FCSTD DOCUMENT  (FreeCAD 0.21R33110 (Git))
Label: FH36W-11S-0.3SHW_1x11-FlatCable
License: All rights reserved
LicenseURL: http://en.wikipedia.org/wiki/All_rights_reserved
objects: Sketcher::SketchObject×17, App::Annotation×2, Part::Part2DObjectPython×2, Image::ImagePlane×1, App::DocumentObjectGroup×1
note: 19 computed .brp shape members not serialized (recipe doc carries the construction recipe); baked Part::Feature solids carry a one-line shape summary decoded from their .brp

FEATURE [Sketcher::SketchObject] Sketch  label="Edge_Cuts_0.05"
  FullyConstrained = true
  Placement = pos=(0,0,0.2) rot=(0,0,1;0rad)
  sketch-geometry (33):
    g0: LineSegment StartX=-2.1 StartY=-2 StartZ=0 EndX=-2.1 EndY=-1.5 EndZ=0
    g1: ArcOfCircle CenterX=-1.9 CenterY=-1.5 CenterZ=0 NormalX=0 NormalY=0 NormalZ=1 AngleXU=0 Radius=0.2 StartAngle=1.5708 EndAngle=3.14159
    g2: ArcOfCircle CenterX=-1.9 CenterY=-1.1 CenterZ=0 NormalX=0 NormalY=0 NormalZ=1 AngleXU=0 Radius=0.2 StartAngle=4.71239 EndAngle=6.28319
    g3: LineSegment StartX=-1.7 StartY=-1.1 StartZ=0 EndX=-1.7 EndY=-0.75 EndZ=0
    g4: ArcOfCircle CenterX=-1.9 CenterY=-0.75 CenterZ=0 NormalX=0 NormalY=0 NormalZ=1 AngleXU=0 Radius=0.2 StartAngle=3e-16 EndAngle=1.5708
    g5: LineSegment StartX=-1.9 StartY=-0.55 StartZ=0 EndX=-2.22 EndY=-0.55 EndZ=0
    g6: ArcOfCircle CenterX=-2.22 CenterY=-0.35 CenterZ=0 NormalX=0 NormalY=0 NormalZ=1 AngleXU=0 Radius=0.2 StartAngle=2.34728 EndAngle=4.71239
    g7: LineSegment StartX=-2.36015 StartY=-0.207323 StartZ=0 EndX=-2.25836 EndY=-0.107324 EndZ=0
    g8: ArcOfCircle CenterX=-2.1182 CenterY=-0.25 CenterZ=0 NormalX=0 NormalY=0 NormalZ=1 AngleXU=0 Radius=0.2 StartAngle=1.5708 EndAngle=2.34728
    g9: ArcOfCircle CenterX=-2 CenterY=0.15 CenterZ=0 NormalX=0 NormalY=0 NormalZ=1 AngleXU=0 Radius=0.2 StartAngle=4.71239 EndAngle=6.28319
    g10: LineSegment StartX=-1.8 StartY=0.15 StartZ=0 EndX=-1.8 EndY=0.9 EndZ=0
    g11: ArcOfCircle CenterX=-1.6 CenterY=0.9 CenterZ=0 NormalX=0 NormalY=0 NormalZ=1 AngleXU=0 Radius=0.2 StartAngle=1.5708 EndAngle=3.14159
    g12: LineSegment StartX=-1.6 StartY=1.1 StartZ=0 EndX=1.6 EndY=1.1 EndZ=0
    g13: ArcOfCircle CenterX=1.6 CenterY=0.9 CenterZ=0 NormalX=0 NormalY=0 NormalZ=1 AngleXU=0 Radius=0.2 StartAngle=1e-16 EndAngle=1.5708
    g14: LineSegment StartX=1.8 StartY=0.9 StartZ=0 EndX=1.8 EndY=0.15 EndZ=0
    g15: ArcOfCircle CenterX=2 CenterY=0.15 CenterZ=0 NormalX=0 NormalY=0 NormalZ=1 AngleXU=0 Radius=0.2 StartAngle=3.14159 EndAngle=4.71239
    g16: LineSegment StartX=2 StartY=-0.05 StartZ=0 EndX=2.1182 EndY=-0.05 EndZ=0
    g17: ArcOfCircle CenterX=2.1182 CenterY=-0.25 CenterZ=0 NormalX=0 NormalY=0 NormalZ=1 AngleXU=0 Radius=0.2 StartAngle=0.794309 EndAngle=1.5708
    g18: LineSegment StartX=2.25836 StartY=-0.107324 StartZ=0 EndX=2.36016 EndY=-0.207324 EndZ=0
    g19: ArcOfCircle CenterX=2.22 CenterY=-0.35 CenterZ=0 NormalX=0 NormalY=0 NormalZ=1 AngleXU=0 Radius=0.2 StartAngle=4.71239 EndAngle=7.07749
    g20: LineSegment StartX=2.22 StartY=-0.55 StartZ=0 EndX=1.9 EndY=-0.55 EndZ=0
    g21: ArcOfCircle CenterX=1.9 CenterY=-0.75 CenterZ=0 NormalX=0 NormalY=0 NormalZ=1 AngleXU=0 Radius=0.2 StartAngle=1.5708 EndAngle=3.14159
    g22: LineSegment StartX=1.7 StartY=-1.1 StartZ=0 EndX=1.7 EndY=-0.75 EndZ=0
    g23: ArcOfCircle CenterX=1.9 CenterY=-1.1 CenterZ=0 NormalX=0 NormalY=0 NormalZ=1 AngleXU=0 Radius=0.2 StartAngle=3.14159 EndAngle=4.71239
    g24: ArcOfCircle CenterX=1.9 CenterY=-1.5 CenterZ=0 NormalX=0 NormalY=0 NormalZ=1 AngleXU=0 Radius=0.2 StartAngle=5e-16 EndAngle=1.5708
    g25: LineSegment StartX=2.1 StartY=-1.5 StartZ=0 EndX=2.1 EndY=-2 EndZ=0
    g26: LineSegment StartX=-2.42 StartY=0.15 StartZ=0 EndX=-2.42 EndY=-0.85 EndZ=0
    g27: LineSegment StartX=2.42 StartY=0.15 StartZ=0 EndX=2.42 EndY=-0.85 EndZ=0
    g28: LineSegment StartX=-2.1182 StartY=-0.05 StartZ=0 EndX=-2 EndY=-0.05 EndZ=0
    g29: LineSegment StartX=2.25836 StartY=-0.107324 StartZ=0 EndX=2.2 EndY=-0.05 EndZ=0
    g30: LineSegment StartX=2.1182 StartY=-0.05 StartZ=0 EndX=2.2 EndY=-0.05 EndZ=0
    g31: LineSegment StartX=-2.25836 StartY=-0.107324 StartZ=0 EndX=-2.2 EndY=-0.05 EndZ=0
    g32: LineSegment StartX=-2.1182 StartY=-0.05 StartZ=0 EndX=-2.2 EndY=-0.05 EndZ=0
  constraints (86):
    c: Vertical(g0)
    c: Vertical(g3)
    c: Horizontal(g5)
    c: Coincident(g8,g7)
    c: Vertical(g10)
    c: Vertical(g14)
    c: Horizontal(g16)
    c: Vertical(g22)
    c: Vertical(g25)
    c: Equal(g25,g0)
    c: Equal(g1,g24)
    c: Equal(g3,g22)
    c: Equal(g5,g20)
    c: Horizontal(g20)
    c: Equal(g18,g7)
    c: Equal(g17,g8)
    c: Equal(g9,g15)
    c: Radius(g1) = 0.2
    c: Equal(g1,g2)
    c: Equal(g2,g4)
    c: Equal(g4,g6)
    c: Equal(g8,g9)
    c: Equal(g11,g24)
    c: Equal(g24,g23)
    c: Equal(g23,g21)
    c: Equal(g21,g19)
    c: Equal(g19,g17)
    c: Tangent(g11,g12) = 1.5708
    c: Tangent(g10,g11) = 1.5708
    c: Tangent(g12,g13) = 1.5708
    c: Tangent(g13,g14) = 1.5708
    c: DistanceX(g10,g13) = 3.6
    c: Tangent(g14,g15) = -1.5708
    c: Tangent(g9,g10) = -1.5708
    c: DistanceY(g15,g12) = 1.15
    c: Symmetric(g11,g12,g-2)
    c: Tangent(g16,g17) = 1.5708
    c: Tangent(g17,g18) = 1.5708
    c: Tangent(g4,g5) = -1.5708
    c: Tangent(g3,g4) = -1.5708
    c: Tangent(g21,g22) = 1.5708
    c: Tangent(g20,g21) = -1.5708
    c: Tangent(g15,g16) = -1.5708
    c: DistanceX(g0,g25) = 4.2
    c: Tangent(g18,g19) = 1.5708
    c: Tangent(g19,g20) = 1.5708
    c: Tangent(g6,g7) = 1.5708
    c: Tangent(g5,g6) = 1.5708
    c: DistanceX(g3,g21) = 3.4
    c: Tangent(g2,g3) = -1.5708
    c: Tangent(g22,g23) = 1.5708
    c: Tangent(g23,g24) = 1.5708
    c: Tangent(g24,g25) = 1.5708
    c: Angle(g2) = 1.5708
    c: Tangent(g1,g2) = 1.5708
    c: Symmetric(g2,g23,g-2)
    c: Tangent(g0,g1) = 1.5708
    c: DistanceY(g5,g11) = 1.65
    c: Angle(g9) = 1.5708
    c: Symmetric(g9,g15,g-2)
    c: Vertical(g26)
    c: Vertical(g27)
    c: Equal(g26,g27)
    c: DistanceX(g26,g27) = 4.84
    c: Symmetric(g26,g27,g-2)
    c: Tangent(g6,g26)
    c: DistanceY(g23,g12) = 2.4
    c: DistanceY(g6,g26) = 0.5
    c: DistanceY(g26,g26) = 1
    c: DistanceY(g0,g0) = 0.5
    c: Coincident(g28,g8)
    c: Coincident(g28,g9)
    c: Horizontal(g28)
    c: Coincident(g29,g17)
    c: Tangent(g29,g17)
    c: Coincident(g30,g16)
    c: Coincident(g30,g29)
    c: Parallel(g30,g16)
    c: Coincident(g31,g7)
    c: Coincident(g32,g8)
    c: Coincident(g32,g31)
    c: Parallel(g31,g7)
    c: DistanceX(g31,g29) = 4.4
    c: Symmetric(g31,g29,g-2)
    c: Equal(g28,g16)
    c: DistanceY(g-1,g11) = 1.1
FEATURE [Sketcher::SketchObject] Sketch003  label="Pads_Poly_F_Cu_padNum=1"
  ExternalGeometry = -> [Sketch]
  FullyConstrained = true
  sketch-geometry (38):
    g0: LineSegment StartX=-1.73 StartY=0.65 StartZ=0 EndX=-1.73 EndY=0.15 EndZ=0
    g1: LineSegment StartX=-1.73 StartY=0.15 StartZ=0 EndX=-1.65 EndY=0.15 EndZ=0
    g2: LineSegment StartX=-1.65 StartY=0.15 StartZ=0 EndX=-1.65 EndY=-0.45 EndZ=0
    g3: LineSegment StartX=-1.65 StartY=-0.45 StartZ=0 EndX=-1.6 EndY=-0.6 EndZ=0
    g4: LineSegment StartX=-1.6 StartY=-0.6 StartZ=0 EndX=-1.6 EndY=-2 EndZ=0
    g5: LineSegment StartX=-1.6 StartY=-2 StartZ=0 EndX=-1.4 EndY=-2 EndZ=0
    g6: LineSegment StartX=-1.4 StartY=-2 StartZ=0 EndX=-1.4 EndY=-0.6 EndZ=0
    g7: LineSegment StartX=-1.4 StartY=-0.6 StartZ=0 EndX=-1.45 EndY=-0.45 EndZ=0
    g8: LineSegment StartX=-1.45 StartY=-0.45 StartZ=0 EndX=-1.45 EndY=0.2 EndZ=0
    g9: LineSegment StartX=-1.45 StartY=0.2 StartZ=0 EndX=-1.35 EndY=0.3 EndZ=0
    g10: LineSegment StartX=-1.35 StartY=0.3 StartZ=0 EndX=-1.35 EndY=0.85 EndZ=0
    g11: LineSegment StartX=-1.4 StartY=0.9 StartZ=0 EndX=-1.6 EndY=0.9 EndZ=0
    g12: LineSegment StartX=-1.65 StartY=0.85 StartZ=0 EndX=-1.65 EndY=0.65 EndZ=0
    g13: ArcOfCircle CenterX=-1.4 CenterY=0.85 CenterZ=0 NormalX=0 NormalY=0 NormalZ=1 AngleXU=0 Radius=0.05 StartAngle=6e-16 EndAngle=1.5708
    g14: LineSegment StartX=-1.65 StartY=0.65 StartZ=0 EndX=-1.73 EndY=0.65 EndZ=0
    g15: ArcOfCircle CenterX=-1.6 CenterY=0.85 CenterZ=0 NormalX=0 NormalY=0 NormalZ=1 AngleXU=0 Radius=0.05 StartAngle=1.5708 EndAngle=3.14159
    g16: GeomPoint X=-1.5 Y=0.9 Z=0
    g17: GeomPoint X=-1.5 Y=-2 Z=0
    g18: LineSegment StartX=1.6 StartY=-2 StartZ=0 EndX=1.6 EndY=-0.6 EndZ=0
    g19: LineSegment StartX=1.6 StartY=-0.6 StartZ=0 EndX=1.65 EndY=-0.45 EndZ=0
    g20: LineSegment StartX=1.65 StartY=-0.45 StartZ=0 EndX=1.65 EndY=0.15 EndZ=0
    g21: LineSegment StartX=1.65 StartY=0.15 StartZ=0 EndX=1.73 EndY=0.15 EndZ=0
    g22: LineSegment StartX=1.73 StartY=0.15 StartZ=0 EndX=1.73 EndY=0.65 EndZ=0
    g23: LineSegment StartX=1.6 StartY=0.9 StartZ=0 EndX=1.4 EndY=0.9 EndZ=0
    g24: LineSegment StartX=1.73 StartY=0.65 StartZ=0 EndX=1.65 EndY=0.65 EndZ=0
    g25: LineSegment StartX=1.65 StartY=0.65 StartZ=0 EndX=1.65 EndY=0.85 EndZ=0
    g26: ArcOfCircle CenterX=1.6 CenterY=0.85 CenterZ=0 NormalX=0 NormalY=0 NormalZ=1 AngleXU=0 Radius=0.05 StartAngle=3e-16 EndAngle=1.5708
    g27: ArcOfCircle CenterX=1.4 CenterY=0.85 CenterZ=0 NormalX=0 NormalY=0 NormalZ=1 AngleXU=0 Radius=0.05 StartAngle=1.5708 EndAngle=3.14159
    g28: LineSegment StartX=1.35 StartY=0.85 StartZ=0 EndX=1.35 EndY=0.3 EndZ=0
    g29: LineSegment StartX=1.35 StartY=0.3 StartZ=0 EndX=1.45 EndY=0.2 EndZ=0
    g30: LineSegment StartX=1.45 StartY=0.2 StartZ=0 EndX=1.45 EndY=-0.45 EndZ=0
    g31: LineSegment StartX=1.45 StartY=-0.45 StartZ=0 EndX=1.4 EndY=-0.6 EndZ=0
    g32: LineSegment StartX=1.4 StartY=-0.6 StartZ=0 EndX=1.4 EndY=-2 EndZ=0
    g33: LineSegment StartX=1.4 StartY=-2 StartZ=0 EndX=1.6 EndY=-2 EndZ=0
    g34: LineSegment StartX=-1.5 StartY=-2 StartZ=0 EndX=0 EndY=-2 EndZ=0
    g35: GeomPoint X=1.5 Y=-2 Z=0
    g36: LineSegment StartX=0 StartY=-2 StartZ=0 EndX=1.5 EndY=-2 EndZ=0
    g37: Circle CenterX=-1.5 CenterY=-1.9 CenterZ=0 NormalX=0 NormalY=0 NormalZ=1 AngleXU=0 Radius=0.0625
  constraints (102):
    c: Vertical(g0)
    c: Coincident(g0,g1)
    c: Coincident(g1,g2)
    c: Vertical(g2)
    c: Coincident(g2,g3)
    c: Coincident(g3,g4)
    c: Vertical(g4)
    c: Coincident(g4,g5)
    c: Horizontal(g5)
    c: Coincident(g5,g6)
    c: Vertical(g6)
    c: Coincident(g6,g7)
    c: Coincident(g7,g8)
    c: Vertical(g8)
    c: Coincident(g8,g9)
    c: Coincident(g9,g10)
    c: Vertical(g10)
    c: Horizontal(g11)
    c: Tangent(g11,g13) = -1.5708
    c: Tangent(g10,g13) = -1.5708
    c: Vertical(g12)
    c: Coincident(g14,g12)
    c: Coincident(g14,g0)
    c: Horizontal(g14)
    c: Tangent(g11,g15) = -1.5708
    c: Tangent(g12,g15) = -1.5708
    c: Equal(g13,g15)
    c: Horizontal(g1)
    c: DistanceY(g0,g0) = 0.5
    c: Symmetric(g11,g11,g16)
    c: Radius(g15) = 0.05
    c: DistanceX(g5,g5) = 0.2
    c: DistanceX(g1,g8) = 0.2
    c: Parallel(g3,g7)
    c: DistanceX(g12,g10) = 0.3
    c: Vertical(g1,g12)
    c: Horizontal(g7,g2)
    c: DistanceY(g3,g2) = 0.15
    c: Symmetric(g4,g5,g17)
    c: DistanceX(g17,g-1) = 1.5
    c: Horizontal(g4,g-10)
    c: Horizontal(g0,g-6)
    c: DistanceX(g-5,g0) = 0.07
    c: DistanceY(g-9,g11) = 1.45
    c: DistanceY(g-9,g2) = 0.1
    c: DistanceX(g-5,g16) = 0.3
    c: DistanceY(g-9,g9) = 0.85
    c: DistanceY(g8,g9) = 0.1
    c: Vertical(g18)
    c: Coincident(g18,g19)
    c: Coincident(g19,g20)
    c: Vertical(g20)
    c: Coincident(g20,g21)
    c: Horizontal(g21)
    c: Coincident(g21,g22)
    c: Vertical(g22)
    c: Horizontal(g23)
    c: Coincident(g22,g24)
    c: Coincident(g24,g25)
    c: Vertical(g25)
    c: Tangent(g25,g26) = -1.5708
    c: Tangent(g23,g27) = -1.5708
    c: Vertical(g28)
    c: Coincident(g28,g29)
    c: Coincident(g29,g30)
    c: Vertical(g30)
    c: Coincident(g30,g31)
    c: Coincident(g31,g32)
    c: Vertical(g32)
    c: Coincident(g33,g32)
    c: Coincident(g33,g18)
    c: Horizontal(g33)
    c: Parallel(g19,g31)
    c: Tangent(g28,g27) = -1.5708
    c: Equal(g26,g27)
    c: Equal(g11,g23)
    c: Equal(g0,g22)
    c: Equal(g14,g24)
    c: Horizontal(g24)
    c: Vertical(g20,g24)
    c: Equal(g29,g9)
    c: Tangent(g23,g26) = -1.5708
    c: DistanceY(g29,g28) = 0.1
    c: Equal(g28,g10)
    c: Equal(g30,g8)
    c: Equal(g31,g7)
    c: Equal(g5,g33)
    c: Equal(g6,g32)
    c: Equal(g4,g18)
    c: Equal(g20,g2)
    c: Symmetric(g11,g23,g-2)
    c: Equal(g25,g12)
    c: Coincident(g34,g17)
    c: PointOnObject(g34,g-2)
    c: Horizontal(g34)
    c: Symmetric(g32,g18,g35)
    c: Coincident(g36,g34)
    c: Coincident(g36,g35)
    c: Horizontal(g36)
    c: Diameter(g37) = 0.125
    c: DistanceY(g17,g37) = 0.1
    c: DistanceX(g17,g37) = 0
FEATURE [Sketcher::SketchObject] Sketch005  label="Pads_Poly_F_Cu_padNum=11"
  FullyConstrained = false
  sketch-geometry (38):
    g0: LineSegment StartX=-1.73 StartY=0.65 StartZ=0 EndX=-1.73 EndY=0.15 EndZ=0
    g1: LineSegment StartX=-1.73 StartY=0.15 StartZ=0 EndX=-1.65 EndY=0.15 EndZ=0
    g2: LineSegment StartX=-1.65 StartY=0.15 StartZ=0 EndX=-1.65 EndY=-0.45 EndZ=0
    g3: LineSegment StartX=-1.65 StartY=-0.45 StartZ=0 EndX=-1.6 EndY=-0.6 EndZ=0
    g4: LineSegment StartX=-1.6 StartY=-0.6 StartZ=0 EndX=-1.6 EndY=-2 EndZ=0
    g5: LineSegment StartX=-1.6 StartY=-2 StartZ=0 EndX=-1.4 EndY=-2 EndZ=0
    g6: LineSegment StartX=-1.4 StartY=-2 StartZ=0 EndX=-1.4 EndY=-0.6 EndZ=0
    g7: LineSegment StartX=-1.4 StartY=-0.6 StartZ=0 EndX=-1.45 EndY=-0.45 EndZ=0
    g8: LineSegment StartX=-1.45 StartY=-0.45 StartZ=0 EndX=-1.45 EndY=0.2 EndZ=0
    g9: LineSegment StartX=-1.45 StartY=0.2 StartZ=0 EndX=-1.35 EndY=0.3 EndZ=0
    g10: LineSegment StartX=-1.35 StartY=0.3 StartZ=0 EndX=-1.35 EndY=0.85 EndZ=0
    g11: LineSegment StartX=-1.4 StartY=0.9 StartZ=0 EndX=-1.6 EndY=0.9 EndZ=0
    g12: LineSegment StartX=-1.65 StartY=0.85 StartZ=0 EndX=-1.65 EndY=0.65 EndZ=0
    g13: ArcOfCircle CenterX=-1.4 CenterY=0.85 CenterZ=0 NormalX=0 NormalY=0 NormalZ=1 AngleXU=0 Radius=0.05 StartAngle=6e-16 EndAngle=1.5708
    g14: LineSegment StartX=-1.65 StartY=0.65 StartZ=0 EndX=-1.73 EndY=0.65 EndZ=0
    g15: ArcOfCircle CenterX=-1.6 CenterY=0.85 CenterZ=0 NormalX=0 NormalY=0 NormalZ=1 AngleXU=0 Radius=0.05 StartAngle=1.5708 EndAngle=3.14159
    g16: GeomPoint X=-1.5 Y=0.9 Z=0
    g17: GeomPoint X=-1.5 Y=-2 Z=0
    g18: LineSegment StartX=1.6 StartY=-2 StartZ=0 EndX=1.6 EndY=-0.6 EndZ=0
    g19: LineSegment StartX=1.6 StartY=-0.6 StartZ=0 EndX=1.65 EndY=-0.45 EndZ=0
    g20: LineSegment StartX=1.65 StartY=-0.45 StartZ=0 EndX=1.65 EndY=0.15 EndZ=0
    g21: LineSegment StartX=1.65 StartY=0.15 StartZ=0 EndX=1.73 EndY=0.15 EndZ=0
    g22: LineSegment StartX=1.73 StartY=0.15 StartZ=0 EndX=1.73 EndY=0.65 EndZ=0
    g23: LineSegment StartX=1.6 StartY=0.9 StartZ=0 EndX=1.4 EndY=0.9 EndZ=0
    g24: LineSegment StartX=1.73 StartY=0.65 StartZ=0 EndX=1.65 EndY=0.65 EndZ=0
    g25: LineSegment StartX=1.65 StartY=0.65 StartZ=0 EndX=1.65 EndY=0.85 EndZ=0
    g26: ArcOfCircle CenterX=1.6 CenterY=0.85 CenterZ=0 NormalX=0 NormalY=0 NormalZ=1 AngleXU=0 Radius=0.05 StartAngle=3e-16 EndAngle=1.5708
    g27: ArcOfCircle CenterX=1.4 CenterY=0.85 CenterZ=0 NormalX=0 NormalY=0 NormalZ=1 AngleXU=0 Radius=0.05 StartAngle=1.5708 EndAngle=3.14159
    g28: LineSegment StartX=1.35 StartY=0.85 StartZ=0 EndX=1.35 EndY=0.3 EndZ=0
    g29: LineSegment StartX=1.35 StartY=0.3 StartZ=0 EndX=1.45 EndY=0.2 EndZ=0
    g30: LineSegment StartX=1.45 StartY=0.2 StartZ=0 EndX=1.45 EndY=-0.45 EndZ=0
    g31: LineSegment StartX=1.45 StartY=-0.45 StartZ=0 EndX=1.4 EndY=-0.6 EndZ=0
    g32: LineSegment StartX=1.4 StartY=-0.6 StartZ=0 EndX=1.4 EndY=-2 EndZ=0
    g33: LineSegment StartX=1.4 StartY=-2 StartZ=0 EndX=1.6 EndY=-2 EndZ=0
    g34: LineSegment StartX=-1.5 StartY=-2 StartZ=0 EndX=0 EndY=-2 EndZ=0
    g35: GeomPoint X=1.5 Y=-2 Z=0
    g36: LineSegment StartX=0 StartY=-2 StartZ=0 EndX=1.5 EndY=-2 EndZ=0
    g37: Circle CenterX=1.5 CenterY=-1.9 CenterZ=0 NormalX=0 NormalY=0 NormalZ=1 AngleXU=0 Radius=0.0625
  constraints (95):
    c: Vertical(g0)
    c: Coincident(g0,g1)
    c: Coincident(g1,g2)
    c: Vertical(g2)
    c: Coincident(g2,g3)
    c: Coincident(g3,g4)
    c: Vertical(g4)
    c: Coincident(g4,g5)
    c: Horizontal(g5)
    c: Coincident(g5,g6)
    c: Vertical(g6)
    c: Coincident(g6,g7)
    c: Coincident(g7,g8)
    c: Vertical(g8)
    c: Coincident(g8,g9)
    c: Coincident(g9,g10)
    c: Vertical(g10)
    c: Horizontal(g11)
    c: Tangent(g11,g13) = -1.5708
    c: Tangent(g10,g13) = -1.5708
    c: Vertical(g12)
    c: Coincident(g14,g12)
    c: Coincident(g14,g0)
    c: Horizontal(g14)
    c: Tangent(g11,g15) = -1.5708
    c: Tangent(g12,g15) = -1.5708
    c: Equal(g13,g15)
    c: Horizontal(g1)
    c: DistanceY(g0,g0) = 0.5
    c: Symmetric(g11,g11,g16)
    c: Radius(g15) = 0.05
    c: DistanceX(g5,g5) = 0.2
    c: DistanceX(g1,g8) = 0.2
    c: Parallel(g3,g7)
    c: DistanceX(g12,g10) = 0.3
    c: Vertical(g1,g12)
    c: Horizontal(g7,g2)
    c: DistanceY(g3,g2) = 0.15
    c: Symmetric(g4,g5,g17)
    c: DistanceX(g17,g-1) = 1.5
    c: DistanceY(g8,g9) = 0.1
    c: Vertical(g18)
    c: Coincident(g18,g19)
    c: Coincident(g19,g20)
    c: Vertical(g20)
    c: Coincident(g20,g21)
    c: Horizontal(g21)
    c: Coincident(g21,g22)
    c: Vertical(g22)
    c: Horizontal(g23)
    c: Coincident(g22,g24)
    c: Coincident(g24,g25)
    c: Vertical(g25)
    c: Tangent(g25,g26) = -1.5708
    c: Tangent(g23,g27) = -1.5708
    c: Vertical(g28)
    c: Coincident(g28,g29)
    c: Coincident(g29,g30)
    c: Vertical(g30)
    c: Coincident(g30,g31)
    c: Coincident(g31,g32)
    c: Vertical(g32)
    c: Coincident(g33,g32)
    c: Coincident(g33,g18)
    c: Horizontal(g33)
    c: Parallel(g19,g31)
    c: Tangent(g28,g27) = -1.5708
    c: Equal(g26,g27)
    c: Equal(g11,g23)
    c: Equal(g0,g22)
    c: Equal(g14,g24)
    c: Horizontal(g24)
    c: Vertical(g20,g24)
    c: Equal(g29,g9)
    c: Tangent(g23,g26) = -1.5708
    c: DistanceY(g29,g28) = 0.1
    c: Equal(g28,g10)
    c: Equal(g30,g8)
    c: Equal(g31,g7)
    c: Equal(g5,g33)
    c: Equal(g6,g32)
    c: Equal(g4,g18)
    c: Equal(g20,g2)
    c: Symmetric(g11,g23,g-2)
    c: Equal(g25,g12)
    c: Coincident(g34,g17)
    c: PointOnObject(g34,g-2)
    c: Horizontal(g34)
    c: Symmetric(g32,g18,g35)
    c: Coincident(g36,g34)
    c: Coincident(g36,g35)
    c: Horizontal(g36)
    c: Diameter(g37) = 0.125
    c: DistanceX(g37,g35) = 0
    c: DistanceY(g35,g37) = 0.1
FEATURE [App::Annotation] Text  label="Ref#_1.0mm"
  LabelText = REF**
  Position = (0,3,0)
FEATURE [App::Annotation] Text001  label="Value#_1.0mm"
  LabelText = Value 
  Position = (0,2,0)
FEATURE [Image::ImagePlane] pads_dimensions  label="pads-dimensions"
  Placement = pos=(-1.63,-0.68,-1) rot=(0,0,1;0rad)
  XSize = 6.21369
  YSize = 4.37753
FEATURE [Sketcher::SketchObject] Sketch006  label="Pads_Poly_F_Cu_padNum=2"
  ExternalGeometry = -> [Sketch003]
  FullyConstrained = false
  sketch-geometry (11):
    g0: LineSegment StartX=-1.29764 StartY=-2 StartZ=0 EndX=-1.29764 EndY=-0.593736 EndZ=0
    g1: LineSegment StartX=-1.29764 StartY=-0.593736 StartZ=0 EndX=-1.34764 EndY=-0.443736 EndZ=0
    g2: LineSegment StartX=-1.34764 StartY=-0.443736 StartZ=0 EndX=-1.34764 EndY=0.208373 EndZ=0
    g3: LineSegment StartX=-1.34764 StartY=0.208373 StartZ=0 EndX=-1.25602 EndY=0.3 EndZ=0
    g4: LineSegment StartX=-1.25602 StartY=0.3 StartZ=0 EndX=-1.13927 EndY=0.3 EndZ=0
    g5: LineSegment StartX=-1.13927 StartY=0.3 StartZ=0 EndX=-1.04764 EndY=0.208373 EndZ=0
    g6: LineSegment StartX=-1.04764 StartY=0.208373 StartZ=0 EndX=-1.04764 EndY=-0.443736 EndZ=0
    g7: LineSegment StartX=-1.04764 StartY=-0.443736 StartZ=0 EndX=-1.09764 EndY=-0.593736 EndZ=0
    g8: LineSegment StartX=-1.09764 StartY=-0.593736 StartZ=0 EndX=-1.09764 EndY=-2 EndZ=0
    g9: LineSegment StartX=-1.09764 StartY=-2 StartZ=0 EndX=-1.29764 EndY=-2 EndZ=0
    g10: Circle CenterX=-1.19764 CenterY=-1.9 CenterZ=0 NormalX=0 NormalY=0 NormalZ=1 AngleXU=0 Radius=0.0625
  constraints (29):
    c: Vertical(g0)
    c: Coincident(g0,g1)
    c: Coincident(g1,g2)
    c: Vertical(g2)
    c: Coincident(g2,g3)
    c: Coincident(g3,g4)
    c: Coincident(g4,g5)
    c: Coincident(g5,g6)
    c: Vertical(g6)
    c: Coincident(g6,g7)
    c: Coincident(g7,g8)
    c: Vertical(g8)
    c: Coincident(g8,g9)
    c: Coincident(g9,g0)
    c: Horizontal(g9)
    c: Horizontal(g4)
    c: Equal(g6,g2)
    c: Equal(g3,g5)
    c: Equal(g1,g7)
    c: Angle(g3) = 0.785398
    c: Angle(g5) = -0.785398
    c: DistanceY(g7,g6) = 0.15
    c: DistanceX(g9,g9) = 0.2
    c: DistanceX(g1,g6) = 0.3
    c: DistanceY(g-3,g0) = 0
    c: DistanceY(g0,g3) = 2.3
    c: Equal(g-4,g10)
    c: DistanceY(g0,g10) = 0.1
    c: DistanceX(g0,g10) = 0.1
FEATURE [Sketcher::SketchObject] Sketch007  label="Pads_Poly_F_Cu_padNum=3"
  FullyConstrained = false
  sketch-geometry (15):
    g0: ArcOfCircle CenterX=-1.00046 CenterY=0.85 CenterZ=0 NormalX=0 NormalY=0 NormalZ=1 AngleXU=0 Radius=0.05 StartAngle=1.57184 EndAngle=3.14159
    g1: LineSegment StartX=-1.05046 StartY=0.85 StartZ=0 EndX=-1.05046 EndY=0.3 EndZ=0
    g2: LineSegment StartX=-1.05046 StartY=0.3 StartZ=0 EndX=-0.961208 EndY=0.198248 EndZ=0
    g3: LineSegment StartX=-0.961208 StartY=0.198248 StartZ=0 EndX=-0.961208 EndY=-0.45 EndZ=0
    g4: LineSegment StartX=-0.961208 StartY=-0.45 StartZ=0 EndX=-1.00121 EndY=-0.601752 EndZ=0
    g5: LineSegment StartX=-1.00121 StartY=-0.601752 StartZ=0 EndX=-1.00121 EndY=-2 EndZ=0
    g6: LineSegment StartX=-1.00121 StartY=-2 StartZ=0 EndX=-0.801208 EndY=-2 EndZ=0
    g7: LineSegment StartX=-0.801208 StartY=-2 StartZ=0 EndX=-0.801208 EndY=-0.601752 EndZ=0
    g8: LineSegment StartX=-0.801208 StartY=-0.601752 StartZ=0 EndX=-0.841208 EndY=-0.45 EndZ=0
    g9: LineSegment StartX=-0.841208 StartY=-0.45 StartZ=0 EndX=-0.841208 EndY=0.2 EndZ=0
    g10: LineSegment StartX=-0.841208 StartY=0.2 StartZ=0 EndX=-0.75 EndY=0.3 EndZ=0
    g11: LineSegment StartX=-0.75 StartY=0.3 StartZ=0 EndX=-0.75 EndY=0.85 EndZ=0
    g12: ArcOfCircle CenterX=-0.8 CenterY=0.85 CenterZ=0 NormalX=0 NormalY=0 NormalZ=1 AngleXU=0 Radius=0.05 StartAngle=1e-15 EndAngle=1.5708
    g13: LineSegment StartX=-0.8 StartY=0.9 StartZ=0 EndX=-1.00051 EndY=0.9 EndZ=0
    g14: Circle CenterX=-0.9 CenterY=-1.9 CenterZ=0 NormalX=0 NormalY=0 NormalZ=1 AngleXU=0 Radius=0.0625
  constraints (29):
    c: Coincident(g0,g1)
    c: Vertical(g1)
    c: Coincident(g1,g2)
    c: Coincident(g2,g3)
    c: Vertical(g3)
    c: Coincident(g3,g4)
    c: Coincident(g4,g5)
    c: Vertical(g5)
    c: Horizontal(g6)
    c: Coincident(g6,g7)
    c: Vertical(g7)
    c: Coincident(g7,g8)
    c: Coincident(g8,g9)
    c: Vertical(g9)
    c: Coincident(g9,g10)
    c: Coincident(g10,g11)
    c: Coincident(g12,g13)
    c: Horizontal(g13)
    c: Coincident(g0,g13)
    c: Equal(g12,g0)
    c: Equal(g11,g1)
    c: DistanceY(g10,g1) = 0
    c: DistanceX(g2,g9) = 0.12
    c: Coincident(g6,g5)
    c: DistanceX(g6,g6) = 0.2
    c: DistanceY(g4,g7) = 0
    c: DistanceY(g3,g8) = 0
    c: Equal(g8,g4)
    c: Equal(g10,g2)
FEATURE [Sketcher::SketchObject] Sketch008  label="Pads_Poly_F_Cu_padNum=4"
  ExternalGeometry = -> [Sketch003]
  FullyConstrained = false
  sketch-geometry (11):
    g0: LineSegment StartX=-0.697644 StartY=-2 StartZ=0 EndX=-0.697644 EndY=-0.593736 EndZ=0
    g1: LineSegment StartX=-0.697644 StartY=-0.593736 StartZ=0 EndX=-0.747644 EndY=-0.443736 EndZ=0
    g2: LineSegment StartX=-0.747644 StartY=-0.443736 StartZ=0 EndX=-0.747644 EndY=0.208373 EndZ=0
    g3: LineSegment StartX=-0.747644 StartY=0.208373 StartZ=0 EndX=-0.656017 EndY=0.3 EndZ=0
    g4: LineSegment StartX=-0.656017 StartY=0.3 StartZ=0 EndX=-0.539272 EndY=0.3 EndZ=0
    g5: LineSegment StartX=-0.539272 StartY=0.3 StartZ=0 EndX=-0.447644 EndY=0.208373 EndZ=0
    g6: LineSegment StartX=-0.447644 StartY=0.208373 StartZ=0 EndX=-0.447644 EndY=-0.443736 EndZ=0
    g7: LineSegment StartX=-0.447644 StartY=-0.443736 StartZ=0 EndX=-0.497644 EndY=-0.593736 EndZ=0
    g8: LineSegment StartX=-0.497644 StartY=-0.593736 StartZ=0 EndX=-0.497644 EndY=-2 EndZ=0
    g9: LineSegment StartX=-0.497644 StartY=-2 StartZ=0 EndX=-0.697644 EndY=-2 EndZ=0
    g10: Circle CenterX=-0.597644 CenterY=-1.9 CenterZ=0 NormalX=0 NormalY=0 NormalZ=1 AngleXU=0 Radius=0.0625
  constraints (29):
    c: Vertical(g0)
    c: Coincident(g0,g1)
    c: Coincident(g1,g2)
    c: Vertical(g2)
    c: Coincident(g2,g3)
    c: Coincident(g3,g4)
    c: Coincident(g4,g5)
    c: Coincident(g5,g6)
    c: Vertical(g6)
    c: Coincident(g6,g7)
    c: Coincident(g7,g8)
    c: Vertical(g8)
    c: Coincident(g8,g9)
    c: Coincident(g9,g0)
    c: Horizontal(g9)
    c: Horizontal(g4)
    c: Equal(g6,g2)
    c: Equal(g3,g5)
    c: Equal(g1,g7)
    c: Angle(g3) = 0.785398
    c: Angle(g5) = -0.785398
    c: DistanceY(g7,g6) = 0.15
    c: DistanceX(g9,g9) = 0.2
    c: DistanceX(g1,g6) = 0.3
    c: DistanceY(g-3,g0) = 0
    c: DistanceY(g0,g3) = 2.3
    c: Equal(g-4,g10)
    c: DistanceY(g0,g10) = 0.1
    c: DistanceX(g0,g10) = 0.1
FEATURE [Sketcher::SketchObject] Sketch009  label="Pads_Poly_F_Cu_padNum=5"
  FullyConstrained = false
  sketch-geometry (15):
    g0: ArcOfCircle CenterX=-0.400457 CenterY=0.85 CenterZ=0 NormalX=0 NormalY=0 NormalZ=1 AngleXU=0 Radius=0.05 StartAngle=1.57184 EndAngle=3.14159
    g1: LineSegment StartX=-0.450457 StartY=0.85 StartZ=0 EndX=-0.450457 EndY=0.3 EndZ=0
    g2: LineSegment StartX=-0.450457 StartY=0.3 StartZ=0 EndX=-0.361208 EndY=0.198248 EndZ=0
    g3: LineSegment StartX=-0.361208 StartY=0.198248 StartZ=0 EndX=-0.361208 EndY=-0.45 EndZ=0
    g4: LineSegment StartX=-0.361208 StartY=-0.45 StartZ=0 EndX=-0.401208 EndY=-0.601752 EndZ=0
    g5: LineSegment StartX=-0.401208 StartY=-0.601752 StartZ=0 EndX=-0.401208 EndY=-2 EndZ=0
    g6: LineSegment StartX=-0.401208 StartY=-2 StartZ=0 EndX=-0.201208 EndY=-2 EndZ=0
    g7: LineSegment StartX=-0.201208 StartY=-2 StartZ=0 EndX=-0.201208 EndY=-0.601752 EndZ=0
    g8: LineSegment StartX=-0.201208 StartY=-0.601752 StartZ=0 EndX=-0.241208 EndY=-0.45 EndZ=0
    g9: LineSegment StartX=-0.241208 StartY=-0.45 StartZ=0 EndX=-0.241208 EndY=0.2 EndZ=0
    g10: LineSegment StartX=-0.241208 StartY=0.2 StartZ=0 EndX=-0.15 EndY=0.3 EndZ=0
    g11: LineSegment StartX=-0.15 StartY=0.3 StartZ=0 EndX=-0.15 EndY=0.85 EndZ=0
    g12: ArcOfCircle CenterX=-0.2 CenterY=0.85 CenterZ=0 NormalX=0 NormalY=0 NormalZ=1 AngleXU=0 Radius=0.05 StartAngle=1e-15 EndAngle=1.5708
    g13: LineSegment StartX=-0.2 StartY=0.9 StartZ=0 EndX=-0.400509 EndY=0.9 EndZ=0
    g14: Circle CenterX=-0.3 CenterY=-1.9 CenterZ=0 NormalX=0 NormalY=0 NormalZ=1 AngleXU=0 Radius=0.0625
  constraints (29):
    c: Coincident(g0,g1)
    c: Vertical(g1)
    c: Coincident(g1,g2)
    c: Coincident(g2,g3)
    c: Vertical(g3)
    c: Coincident(g3,g4)
    c: Coincident(g4,g5)
    c: Vertical(g5)
    c: Horizontal(g6)
    c: Coincident(g6,g7)
    c: Vertical(g7)
    c: Coincident(g7,g8)
    c: Coincident(g8,g9)
    c: Vertical(g9)
    c: Coincident(g9,g10)
    c: Coincident(g10,g11)
    c: Coincident(g12,g13)
    c: Horizontal(g13)
    c: Coincident(g0,g13)
    c: Equal(g12,g0)
    c: Equal(g11,g1)
    c: DistanceY(g10,g1) = 0
    c: DistanceX(g2,g9) = 0.12
    c: Coincident(g6,g5)
    c: DistanceX(g6,g6) = 0.2
    c: DistanceY(g4,g7) = 0
    c: DistanceY(g3,g8) = 0
    c: Equal(g8,g4)
    c: Equal(g10,g2)
FEATURE [Sketcher::SketchObject] Sketch010  label="Pads_Poly_F_Cu_padNum=6"
  ExternalGeometry = -> [Sketch003]
  FullyConstrained = false
  sketch-geometry (11):
    g0: LineSegment StartX=-0.097644 StartY=-2 StartZ=0 EndX=-0.097644 EndY=-0.593736 EndZ=0
    g1: LineSegment StartX=-0.097644 StartY=-0.593736 StartZ=0 EndX=-0.147644 EndY=-0.443736 EndZ=0
    g2: LineSegment StartX=-0.147644 StartY=-0.443736 StartZ=0 EndX=-0.147644 EndY=0.208373 EndZ=0
    g3: LineSegment StartX=-0.147644 StartY=0.208373 StartZ=0 EndX=-0.0560169 EndY=0.3 EndZ=0
    g4: LineSegment StartX=-0.0560169 StartY=0.3 StartZ=0 EndX=0.0607283 EndY=0.3 EndZ=0
    g5: LineSegment StartX=0.0607283 StartY=0.3 StartZ=0 EndX=0.152356 EndY=0.208373 EndZ=0
    g6: LineSegment StartX=0.152356 StartY=0.208373 StartZ=0 EndX=0.152356 EndY=-0.443736 EndZ=0
    g7: LineSegment StartX=0.152356 StartY=-0.443736 StartZ=0 EndX=0.102356 EndY=-0.593736 EndZ=0
    g8: LineSegment StartX=0.102356 StartY=-0.593736 StartZ=0 EndX=0.102356 EndY=-2 EndZ=0
    g9: LineSegment StartX=0.102356 StartY=-2 StartZ=0 EndX=-0.097644 EndY=-2 EndZ=0
    g10: Circle CenterX=0.002356 CenterY=-1.9 CenterZ=0 NormalX=0 NormalY=0 NormalZ=1 AngleXU=0 Radius=0.0625
  constraints (29):
    c: Vertical(g0)
    c: Coincident(g0,g1)
    c: Coincident(g1,g2)
    c: Vertical(g2)
    c: Coincident(g2,g3)
    c: Coincident(g3,g4)
    c: Coincident(g4,g5)
    c: Coincident(g5,g6)
    c: Vertical(g6)
    c: Coincident(g6,g7)
    c: Coincident(g7,g8)
    c: Vertical(g8)
    c: Coincident(g8,g9)
    c: Coincident(g9,g0)
    c: Horizontal(g9)
    c: Horizontal(g4)
    c: Equal(g6,g2)
    c: Equal(g3,g5)
    c: Equal(g1,g7)
    c: Angle(g3) = 0.785398
    c: Angle(g5) = -0.785398
    c: DistanceY(g7,g6) = 0.15
    c: DistanceX(g9,g9) = 0.2
    c: DistanceX(g1,g6) = 0.3
    c: DistanceY(g-3,g0) = 0
    c: DistanceY(g0,g3) = 2.3
    c: Equal(g-4,g10)
    c: DistanceY(g0,g10) = 0.1
    c: DistanceX(g0,g10) = 0.1
FEATURE [Sketcher::SketchObject] Sketch011  label="Pads_Poly_F_Cu_padNum=7"
  FullyConstrained = false
  sketch-geometry (15):
    g0: ArcOfCircle CenterX=0.199543 CenterY=0.85 CenterZ=0 NormalX=0 NormalY=0 NormalZ=1 AngleXU=0 Radius=0.05 StartAngle=1.57184 EndAngle=3.14159
    g1: LineSegment StartX=0.149543 StartY=0.85 StartZ=0 EndX=0.149543 EndY=0.3 EndZ=0
    g2: LineSegment StartX=0.149543 StartY=0.3 StartZ=0 EndX=0.238792 EndY=0.198248 EndZ=0
    g3: LineSegment StartX=0.238792 StartY=0.198248 StartZ=0 EndX=0.238792 EndY=-0.45 EndZ=0
    g4: LineSegment StartX=0.238792 StartY=-0.45 StartZ=0 EndX=0.198792 EndY=-0.601752 EndZ=0
    g5: LineSegment StartX=0.198792 StartY=-0.601752 StartZ=0 EndX=0.198792 EndY=-2 EndZ=0
    g6: LineSegment StartX=0.198792 StartY=-2 StartZ=0 EndX=0.398792 EndY=-2 EndZ=0
    g7: LineSegment StartX=0.398792 StartY=-2 StartZ=0 EndX=0.398792 EndY=-0.601752 EndZ=0
    g8: LineSegment StartX=0.398792 StartY=-0.601752 StartZ=0 EndX=0.358792 EndY=-0.45 EndZ=0
    g9: LineSegment StartX=0.358792 StartY=-0.45 StartZ=0 EndX=0.358792 EndY=0.2 EndZ=0
    g10: LineSegment StartX=0.358792 StartY=0.2 StartZ=0 EndX=0.45 EndY=0.3 EndZ=0
    g11: LineSegment StartX=0.45 StartY=0.3 StartZ=0 EndX=0.45 EndY=0.85 EndZ=0
    g12: ArcOfCircle CenterX=0.4 CenterY=0.85 CenterZ=0 NormalX=0 NormalY=0 NormalZ=1 AngleXU=0 Radius=0.05 StartAngle=1e-15 EndAngle=1.5708
    g13: LineSegment StartX=0.4 StartY=0.9 StartZ=0 EndX=0.199491 EndY=0.9 EndZ=0
    g14: Circle CenterX=0.3 CenterY=-1.9 CenterZ=0 NormalX=0 NormalY=0 NormalZ=1 AngleXU=0 Radius=0.0625
  constraints (29):
    c: Coincident(g0,g1)
    c: Vertical(g1)
    c: Coincident(g1,g2)
    c: Coincident(g2,g3)
    c: Vertical(g3)
    c: Coincident(g3,g4)
    c: Coincident(g4,g5)
    c: Vertical(g5)
    c: Horizontal(g6)
    c: Coincident(g6,g7)
    c: Vertical(g7)
    c: Coincident(g7,g8)
    c: Coincident(g8,g9)
    c: Vertical(g9)
    c: Coincident(g9,g10)
    c: Coincident(g10,g11)
    c: Coincident(g12,g13)
    c: Horizontal(g13)
    c: Coincident(g0,g13)
    c: Equal(g12,g0)
    c: Equal(g11,g1)
    c: DistanceY(g10,g1) = 0
    c: DistanceX(g2,g9) = 0.12
    c: Coincident(g6,g5)
    c: DistanceX(g6,g6) = 0.2
    c: DistanceY(g4,g7) = 0
    c: DistanceY(g3,g8) = 0
    c: Equal(g8,g4)
    c: Equal(g10,g2)
FEATURE [Sketcher::SketchObject] Sketch012  label="Pads_Poly_F_Cu_padNum=8"
  ExternalGeometry = -> [Sketch003]
  FullyConstrained = false
  sketch-geometry (11):
    g0: LineSegment StartX=0.502356 StartY=-2 StartZ=0 EndX=0.502356 EndY=-0.593736 EndZ=0
    g1: LineSegment StartX=0.502356 StartY=-0.593736 StartZ=0 EndX=0.452356 EndY=-0.443736 EndZ=0
    g2: LineSegment StartX=0.452356 StartY=-0.443736 StartZ=0 EndX=0.452356 EndY=0.208373 EndZ=0
    g3: LineSegment StartX=0.452356 StartY=0.208373 StartZ=0 EndX=0.543983 EndY=0.3 EndZ=0
    g4: LineSegment StartX=0.543983 StartY=0.3 StartZ=0 EndX=0.660728 EndY=0.3 EndZ=0
    g5: LineSegment StartX=0.660728 StartY=0.3 StartZ=0 EndX=0.752356 EndY=0.208373 EndZ=0
    g6: LineSegment StartX=0.752356 StartY=0.208373 StartZ=0 EndX=0.752356 EndY=-0.443736 EndZ=0
    g7: LineSegment StartX=0.752356 StartY=-0.443736 StartZ=0 EndX=0.702356 EndY=-0.593736 EndZ=0
    g8: LineSegment StartX=0.702356 StartY=-0.593736 StartZ=0 EndX=0.702356 EndY=-2 EndZ=0
    g9: LineSegment StartX=0.702356 StartY=-2 StartZ=0 EndX=0.502356 EndY=-2 EndZ=0
    g10: Circle CenterX=0.602356 CenterY=-1.9 CenterZ=0 NormalX=0 NormalY=0 NormalZ=1 AngleXU=0 Radius=0.0625
  constraints (29):
    c: Vertical(g0)
    c: Coincident(g0,g1)
    c: Coincident(g1,g2)
    c: Vertical(g2)
    c: Coincident(g2,g3)
    c: Coincident(g3,g4)
    c: Coincident(g4,g5)
    c: Coincident(g5,g6)
    c: Vertical(g6)
    c: Coincident(g6,g7)
    c: Coincident(g7,g8)
    c: Vertical(g8)
    c: Coincident(g8,g9)
    c: Coincident(g9,g0)
    c: Horizontal(g9)
    c: Horizontal(g4)
    c: Equal(g6,g2)
    c: Equal(g3,g5)
    c: Equal(g1,g7)
    c: Angle(g3) = 0.785398
    c: Angle(g5) = -0.785398
    c: DistanceY(g7,g6) = 0.15
    c: DistanceX(g9,g9) = 0.2
    c: DistanceX(g1,g6) = 0.3
    c: DistanceY(g-3,g0) = 0
    c: DistanceY(g0,g3) = 2.3
    c: Equal(g-4,g10)
    c: DistanceY(g0,g10) = 0.1
    c: DistanceX(g0,g10) = 0.1
FEATURE [Sketcher::SketchObject] Sketch013  label="Pads_Poly_F_Cu_padNum=9"
  FullyConstrained = false
  sketch-geometry (15):
    g0: ArcOfCircle CenterX=0.799543 CenterY=0.85 CenterZ=0 NormalX=0 NormalY=0 NormalZ=1 AngleXU=0 Radius=0.05 StartAngle=1.57184 EndAngle=3.14159
    g1: LineSegment StartX=0.749543 StartY=0.85 StartZ=0 EndX=0.749543 EndY=0.3 EndZ=0
    g2: LineSegment StartX=0.749543 StartY=0.3 StartZ=0 EndX=0.838792 EndY=0.198248 EndZ=0
    g3: LineSegment StartX=0.838792 StartY=0.198248 StartZ=0 EndX=0.838792 EndY=-0.45 EndZ=0
    g4: LineSegment StartX=0.838792 StartY=-0.45 StartZ=0 EndX=0.798792 EndY=-0.601752 EndZ=0
    g5: LineSegment StartX=0.798792 StartY=-0.601752 StartZ=0 EndX=0.798792 EndY=-2 EndZ=0
    g6: LineSegment StartX=0.798792 StartY=-2 StartZ=0 EndX=0.998792 EndY=-2 EndZ=0
    g7: LineSegment StartX=0.998792 StartY=-2 StartZ=0 EndX=0.998792 EndY=-0.601752 EndZ=0
    g8: LineSegment StartX=0.998792 StartY=-0.601752 StartZ=0 EndX=0.958792 EndY=-0.45 EndZ=0
    g9: LineSegment StartX=0.958792 StartY=-0.45 StartZ=0 EndX=0.958792 EndY=0.2 EndZ=0
    g10: LineSegment StartX=0.958792 StartY=0.2 StartZ=0 EndX=1.05 EndY=0.3 EndZ=0
    g11: LineSegment StartX=1.05 StartY=0.3 StartZ=0 EndX=1.05 EndY=0.85 EndZ=0
    g12: ArcOfCircle CenterX=1 CenterY=0.85 CenterZ=0 NormalX=0 NormalY=0 NormalZ=1 AngleXU=0 Radius=0.05 StartAngle=1e-15 EndAngle=1.5708
    g13: LineSegment StartX=1 StartY=0.9 StartZ=0 EndX=0.799491 EndY=0.9 EndZ=0
    g14: Circle CenterX=0.9 CenterY=-1.9 CenterZ=0 NormalX=0 NormalY=0 NormalZ=1 AngleXU=0 Radius=0.0625
  constraints (29):
    c: Coincident(g0,g1)
    c: Vertical(g1)
    c: Coincident(g1,g2)
    c: Coincident(g2,g3)
    c: Vertical(g3)
    c: Coincident(g3,g4)
    c: Coincident(g4,g5)
    c: Vertical(g5)
    c: Horizontal(g6)
    c: Coincident(g6,g7)
    c: Vertical(g7)
    c: Coincident(g7,g8)
    c: Coincident(g8,g9)
    c: Vertical(g9)
    c: Coincident(g9,g10)
    c: Coincident(g10,g11)
    c: Coincident(g12,g13)
    c: Horizontal(g13)
    c: Coincident(g0,g13)
    c: Equal(g12,g0)
    c: Equal(g11,g1)
    c: DistanceY(g10,g1) = 0
    c: DistanceX(g2,g9) = 0.12
    c: Coincident(g6,g5)
    c: DistanceX(g6,g6) = 0.2
    c: DistanceY(g4,g7) = 0
    c: DistanceY(g3,g8) = 0
    c: Equal(g8,g4)
    c: Equal(g10,g2)
FEATURE [Sketcher::SketchObject] Sketch014  label="Pads_Poly_F_Cu_padNum=10"
  ExternalGeometry = -> [Sketch003]
  FullyConstrained = false
  sketch-geometry (11):
    g0: LineSegment StartX=1.10236 StartY=-2 StartZ=0 EndX=1.10236 EndY=-0.593736 EndZ=0
    g1: LineSegment StartX=1.10236 StartY=-0.593736 StartZ=0 EndX=1.05236 EndY=-0.443736 EndZ=0
    g2: LineSegment StartX=1.05236 StartY=-0.443736 StartZ=0 EndX=1.05236 EndY=0.208373 EndZ=0
    g3: LineSegment StartX=1.05236 StartY=0.208373 StartZ=0 EndX=1.14398 EndY=0.3 EndZ=0
    g4: LineSegment StartX=1.14398 StartY=0.3 StartZ=0 EndX=1.26073 EndY=0.3 EndZ=0
    g5: LineSegment StartX=1.26073 StartY=0.3 StartZ=0 EndX=1.35236 EndY=0.208373 EndZ=0
    g6: LineSegment StartX=1.35236 StartY=0.208373 StartZ=0 EndX=1.35236 EndY=-0.443736 EndZ=0
    g7: LineSegment StartX=1.35236 StartY=-0.443736 StartZ=0 EndX=1.30236 EndY=-0.593736 EndZ=0
    g8: LineSegment StartX=1.30236 StartY=-0.593736 StartZ=0 EndX=1.30236 EndY=-2 EndZ=0
    g9: LineSegment StartX=1.30236 StartY=-2 StartZ=0 EndX=1.10236 EndY=-2 EndZ=0
    g10: Circle CenterX=1.20236 CenterY=-1.9 CenterZ=0 NormalX=0 NormalY=0 NormalZ=1 AngleXU=0 Radius=0.0625
  constraints (29):
    c: Vertical(g0)
    c: Coincident(g0,g1)
    c: Coincident(g1,g2)
    c: Vertical(g2)
    c: Coincident(g2,g3)
    c: Coincident(g3,g4)
    c: Coincident(g4,g5)
    c: Coincident(g5,g6)
    c: Vertical(g6)
    c: Coincident(g6,g7)
    c: Coincident(g7,g8)
    c: Vertical(g8)
    c: Coincident(g8,g9)
    c: Coincident(g9,g0)
    c: Horizontal(g9)
    c: Horizontal(g4)
    c: Equal(g6,g2)
    c: Equal(g3,g5)
    c: Equal(g1,g7)
    c: Angle(g3) = 0.785398
    c: Angle(g5) = -0.785398
    c: DistanceY(g7,g6) = 0.15
    c: DistanceX(g9,g9) = 0.2
    c: DistanceX(g1,g6) = 0.3
    c: DistanceY(g-3,g0) = 0
    c: DistanceY(g0,g3) = 2.3
    c: Equal(g-4,g10)
    c: DistanceY(g0,g10) = 0.1
    c: DistanceX(g0,g10) = 0.1
FEATURE [Sketcher::SketchObject] Sketch022  label="FZ_F_Mask_low"
  FullyConstrained = false
  sketch-geometry (40):
    g0: LineSegment StartX=-1.29764 StartY=-0.593736 StartZ=0 EndX=-1.34764 EndY=-0.443736 EndZ=0
    g1: LineSegment StartX=-1.34764 StartY=-0.443736 StartZ=0 EndX=-1.34764 EndY=0.208373 EndZ=0
    g2: LineSegment StartX=-1.34764 StartY=0.208373 StartZ=0 EndX=-1.25602 EndY=0.3 EndZ=0
    g3: LineSegment StartX=-1.25602 StartY=0.3 StartZ=0 EndX=-1.13927 EndY=0.3 EndZ=0
    g4: LineSegment StartX=-1.13927 StartY=0.3 StartZ=0 EndX=-1.04764 EndY=0.208373 EndZ=0
    g5: LineSegment StartX=-1.04764 StartY=0.208373 StartZ=0 EndX=-1.04764 EndY=-0.443736 EndZ=0
    g6: LineSegment StartX=-1.04764 StartY=-0.443736 StartZ=0 EndX=-1.09764 EndY=-0.593736 EndZ=0
    g7: LineSegment StartX=-1.09764 StartY=-0.593736 StartZ=0 EndX=-1.29764 EndY=-0.593736 EndZ=0
    g8: LineSegment StartX=-0.697644 StartY=-0.593736 StartZ=0 EndX=-0.747644 EndY=-0.443736 EndZ=0
    g9: LineSegment StartX=-0.747644 StartY=-0.443736 StartZ=0 EndX=-0.747644 EndY=0.208373 EndZ=0
    g10: LineSegment StartX=-0.747644 StartY=0.208373 StartZ=0 EndX=-0.656017 EndY=0.3 EndZ=0
    g11: LineSegment StartX=-0.656017 StartY=0.3 StartZ=0 EndX=-0.539272 EndY=0.3 EndZ=0
    g12: LineSegment StartX=-0.539272 StartY=0.3 StartZ=0 EndX=-0.447644 EndY=0.208373 EndZ=0
    g13: LineSegment StartX=-0.447644 StartY=0.208373 StartZ=0 EndX=-0.447644 EndY=-0.443736 EndZ=0
    g14: LineSegment StartX=-0.447644 StartY=-0.443736 StartZ=0 EndX=-0.497644 EndY=-0.593736 EndZ=0
    g15: LineSegment StartX=-0.497644 StartY=-0.593736 StartZ=0 EndX=-0.697644 EndY=-0.593736 EndZ=0
    g16: LineSegment StartX=-0.097644 StartY=-0.593736 StartZ=0 EndX=-0.147644 EndY=-0.443736 EndZ=0
    g17: LineSegment StartX=-0.147644 StartY=-0.443736 StartZ=0 EndX=-0.147644 EndY=0.208373 EndZ=0
    g18: LineSegment StartX=-0.147644 StartY=0.208373 StartZ=0 EndX=-0.0560169 EndY=0.3 EndZ=0
    g19: LineSegment StartX=-0.0560169 StartY=0.3 StartZ=0 EndX=0.0607283 EndY=0.3 EndZ=0
    g20: LineSegment StartX=0.0607283 StartY=0.3 StartZ=0 EndX=0.152356 EndY=0.208373 EndZ=0
    g21: LineSegment StartX=0.152356 StartY=0.208373 StartZ=0 EndX=0.152356 EndY=-0.443736 EndZ=0
    g22: LineSegment StartX=0.152356 StartY=-0.443736 StartZ=0 EndX=0.102356 EndY=-0.593736 EndZ=0
    g23: LineSegment StartX=0.102356 StartY=-0.593736 StartZ=0 EndX=-0.097644 EndY=-0.593736 EndZ=0
    g24: LineSegment StartX=0.502356 StartY=-0.593736 StartZ=0 EndX=0.452356 EndY=-0.443736 EndZ=0
    g25: LineSegment StartX=0.452356 StartY=-0.443736 StartZ=0 EndX=0.452356 EndY=0.208373 EndZ=0
    g26: LineSegment StartX=0.452356 StartY=0.208373 StartZ=0 EndX=0.543983 EndY=0.3 EndZ=0
    g27: LineSegment StartX=0.543983 StartY=0.3 StartZ=0 EndX=0.660728 EndY=0.3 EndZ=0
    g28: LineSegment StartX=0.660728 StartY=0.3 StartZ=0 EndX=0.752356 EndY=0.208373 EndZ=0
    g29: LineSegment StartX=0.752356 StartY=0.208373 StartZ=0 EndX=0.752356 EndY=-0.443736 EndZ=0
    g30: LineSegment StartX=0.752356 StartY=-0.443736 StartZ=0 EndX=0.702356 EndY=-0.593736 EndZ=0
    g31: LineSegment StartX=0.702356 StartY=-0.593736 StartZ=0 EndX=0.502356 EndY=-0.593736 EndZ=0
    g32: LineSegment StartX=1.10236 StartY=-0.593736 StartZ=0 EndX=1.05236 EndY=-0.443736 EndZ=0
    g33: LineSegment StartX=1.05236 StartY=-0.443736 StartZ=0 EndX=1.05236 EndY=0.208373 EndZ=0
    g34: LineSegment StartX=1.05236 StartY=0.208373 StartZ=0 EndX=1.14398 EndY=0.3 EndZ=0
    g35: LineSegment StartX=1.14398 StartY=0.3 StartZ=0 EndX=1.26073 EndY=0.3 EndZ=0
    g36: LineSegment StartX=1.26073 StartY=0.3 StartZ=0 EndX=1.35236 EndY=0.208373 EndZ=0
    g37: LineSegment StartX=1.35236 StartY=0.208373 StartZ=0 EndX=1.35236 EndY=-0.443736 EndZ=0
    g38: LineSegment StartX=1.35236 StartY=-0.443736 StartZ=0 EndX=1.30236 EndY=-0.593736 EndZ=0
    g39: LineSegment StartX=1.30236 StartY=-0.593736 StartZ=0 EndX=1.10236 EndY=-0.593736 EndZ=0
  constraints (60):
    c: Coincident(g0,g1)
    c: Vertical(g1)
    c: Coincident(g1,g2)
    c: Coincident(g2,g3)
    c: Horizontal(g3)
    c: Coincident(g3,g4)
    c: Coincident(g4,g5)
    c: Vertical(g5)
    c: Coincident(g5,g6)
    c: Horizontal(g7)
    c: Coincident(g0,g7)
    c: Block(g7)
    c: Coincident(g8,g9)
    c: Vertical(g9)
    c: Coincident(g9,g10)
    c: Coincident(g10,g11)
    c: Horizontal(g11)
    c: Coincident(g11,g12)
    c: Coincident(g12,g13)
    c: Vertical(g13)
    c: Coincident(g13,g14)
    c: Horizontal(g15)
    c: Coincident(g8,g15)
    c: Block(g15)
    c: Coincident(g16,g17)
    c: Vertical(g17)
    c: Coincident(g17,g18)
    c: Coincident(g18,g19)
    c: Horizontal(g19)
    c: Coincident(g19,g20)
    c: Coincident(g20,g21)
    c: Vertical(g21)
    c: Coincident(g21,g22)
    c: Horizontal(g23)
    c: Coincident(g16,g23)
    c: Block(g23)
    c: Coincident(g24,g25)
    c: Vertical(g25)
    c: Coincident(g25,g26)
    c: Coincident(g26,g27)
    c: Horizontal(g27)
    c: Coincident(g27,g28)
    c: Coincident(g28,g29)
    c: Vertical(g29)
    c: Coincident(g29,g30)
    c: Horizontal(g31)
    c: Coincident(g24,g31)
    c: Block(g31)
    c: Coincident(g32,g33)
    c: Vertical(g33)
    c: Coincident(g33,g34)
    c: Coincident(g34,g35)
    c: Horizontal(g35)
    c: Coincident(g35,g36)
    c: Coincident(g36,g37)
    c: Vertical(g37)
    c: Coincident(g37,g38)
    c: Horizontal(g39)
    c: Coincident(g32,g39)
    c: Block(g39)
FEATURE [Sketcher::SketchObject] Sketch029  label="FZ_F_Mask_up"
  FullyConstrained = false
  sketch-geometry (52):
    g0: LineSegment StartX=-1.73 StartY=0.65 StartZ=0 EndX=-1.73 EndY=0.15 EndZ=0
    g1: LineSegment StartX=-1.73 StartY=0.15 StartZ=0 EndX=-1.45 EndY=0.15 EndZ=0
    g2: LineSegment StartX=-1.45 StartY=0.2 StartZ=0 EndX=-1.35 EndY=0.3 EndZ=0
    g3: LineSegment StartX=-1.35 StartY=0.3 StartZ=0 EndX=-1.35 EndY=0.85 EndZ=0
    g4: ArcOfCircle CenterX=-1.4 CenterY=0.85 CenterZ=0 NormalX=0 NormalY=0 NormalZ=1 AngleXU=0 Radius=0.05 StartAngle=6e-16 EndAngle=1.5708
    g5: LineSegment StartX=-1.4 StartY=0.9 StartZ=0 EndX=-1.6 EndY=0.9 EndZ=0
    g6: ArcOfCircle CenterX=-1.6 CenterY=0.85 CenterZ=0 NormalX=0 NormalY=0 NormalZ=1 AngleXU=0 Radius=0.05 StartAngle=1.5708 EndAngle=3.14159
    g7: LineSegment StartX=-1.65 StartY=0.85 StartZ=0 EndX=-1.65 EndY=0.65 EndZ=0
    g8: LineSegment StartX=-1.65 StartY=0.65 StartZ=0 EndX=-1.73 EndY=0.65 EndZ=0
    g9: LineSegment StartX=-1.45 StartY=0.2 StartZ=0 EndX=-1.45 EndY=0.15 EndZ=0
    g10: LineSegment StartX=1.45 StartY=0.15 StartZ=0 EndX=1.73 EndY=0.15 EndZ=0
    g11: LineSegment StartX=1.73 StartY=0.15 StartZ=0 EndX=1.73 EndY=0.65 EndZ=0
    g12: LineSegment StartX=1.73 StartY=0.65 StartZ=0 EndX=1.65 EndY=0.65 EndZ=0
    g13: LineSegment StartX=1.65 StartY=0.65 StartZ=0 EndX=1.65 EndY=0.85 EndZ=0
    g14: ArcOfCircle CenterX=1.6 CenterY=0.85 CenterZ=0 NormalX=0 NormalY=0 NormalZ=1 AngleXU=0 Radius=0.05 StartAngle=0 EndAngle=1.5708
    g15: LineSegment StartX=1.6 StartY=0.9 StartZ=0 EndX=1.4 EndY=0.9 EndZ=0
    g16: ArcOfCircle CenterX=1.4 CenterY=0.85 CenterZ=0 NormalX=0 NormalY=0 NormalZ=1 AngleXU=0 Radius=0.05 StartAngle=1.5708 EndAngle=3.14159
    g17: LineSegment StartX=1.35 StartY=0.85 StartZ=0 EndX=1.35 EndY=0.3 EndZ=0
    g18: LineSegment StartX=1.35 StartY=0.3 StartZ=0 EndX=1.45 EndY=0.2 EndZ=0
    g19: LineSegment StartX=1.45 StartY=0.2 StartZ=0 EndX=1.45 EndY=0.15 EndZ=0
    g20: ArcOfCircle CenterX=-1.00046 CenterY=0.85 CenterZ=0 NormalX=0 NormalY=0 NormalZ=1 AngleXU=0 Radius=0.05 StartAngle=1.57184 EndAngle=3.14159
    g21: LineSegment StartX=-1.05046 StartY=0.85 StartZ=0 EndX=-1.05046 EndY=0.3 EndZ=0
    g22: LineSegment StartX=-1.05046 StartY=0.3 StartZ=0 EndX=-0.961208 EndY=0.2 EndZ=0
    g23: LineSegment StartX=-0.841208 StartY=0.2 StartZ=0 EndX=-0.75 EndY=0.3 EndZ=0
    g24: LineSegment StartX=-0.75 StartY=0.3 StartZ=0 EndX=-0.75 EndY=0.85 EndZ=0
    g25: ArcOfCircle CenterX=-0.8 CenterY=0.85 CenterZ=0 NormalX=0 NormalY=0 NormalZ=1 AngleXU=0 Radius=0.05 StartAngle=1e-15 EndAngle=1.5708
    g26: LineSegment StartX=-0.8 StartY=0.9 StartZ=0 EndX=-1.00051 EndY=0.9 EndZ=0
    g27: LineSegment StartX=-0.961208 StartY=0.2 StartZ=0 EndX=-0.841208 EndY=0.2 EndZ=0
    g28: ArcOfCircle CenterX=-0.400457 CenterY=0.85 CenterZ=0 NormalX=0 NormalY=0 NormalZ=1 AngleXU=0 Radius=0.05 StartAngle=1.57184 EndAngle=3.14159
    g29: LineSegment StartX=-0.450457 StartY=0.85 StartZ=0 EndX=-0.450457 EndY=0.3 EndZ=0
    g30: LineSegment StartX=-0.450457 StartY=0.3 StartZ=0 EndX=-0.361208 EndY=0.2 EndZ=0
    g31: LineSegment StartX=-0.241208 StartY=0.2 StartZ=0 EndX=-0.15 EndY=0.3 EndZ=0
    g32: LineSegment StartX=-0.15 StartY=0.3 StartZ=0 EndX=-0.15 EndY=0.85 EndZ=0
    g33: ArcOfCircle CenterX=-0.2 CenterY=0.85 CenterZ=0 NormalX=0 NormalY=0 NormalZ=1 AngleXU=0 Radius=0.05 StartAngle=1e-15 EndAngle=1.5708
    g34: LineSegment StartX=-0.2 StartY=0.9 StartZ=0 EndX=-0.400509 EndY=0.9 EndZ=0
    g35: LineSegment StartX=-0.361208 StartY=0.2 StartZ=0 EndX=-0.241208 EndY=0.2 EndZ=0
    g36: ArcOfCircle CenterX=0.199543 CenterY=0.85 CenterZ=0 NormalX=0 NormalY=0 NormalZ=1 AngleXU=0 Radius=0.05 StartAngle=1.57184 EndAngle=3.14159
    g37: LineSegment StartX=0.149543 StartY=0.85 StartZ=0 EndX=0.149543 EndY=0.3 EndZ=0
    g38: LineSegment StartX=0.149543 StartY=0.3 StartZ=0 EndX=0.238792 EndY=0.2 EndZ=0
    g39: LineSegment StartX=0.358792 StartY=0.2 StartZ=0 EndX=0.45 EndY=0.3 EndZ=0
    g40: LineSegment StartX=0.45 StartY=0.3 StartZ=0 EndX=0.45 EndY=0.85 EndZ=0
    g41: ArcOfCircle CenterX=0.4 CenterY=0.85 CenterZ=0 NormalX=0 NormalY=0 NormalZ=1 AngleXU=0 Radius=0.05 StartAngle=1e-15 EndAngle=1.5708
    g42: LineSegment StartX=0.4 StartY=0.9 StartZ=0 EndX=0.199491 EndY=0.9 EndZ=0
    g43: LineSegment StartX=0.238792 StartY=0.2 StartZ=0 EndX=0.358792 EndY=0.2 EndZ=0
    g44: ArcOfCircle CenterX=0.799543 CenterY=0.85 CenterZ=0 NormalX=0 NormalY=0 NormalZ=1 AngleXU=0 Radius=0.05 StartAngle=1.57184 EndAngle=3.14159
    g45: LineSegment StartX=0.749543 StartY=0.85 StartZ=0 EndX=0.749543 EndY=0.3 EndZ=0
    g46: LineSegment StartX=0.749543 StartY=0.3 StartZ=0 EndX=0.838792 EndY=0.2 EndZ=0
    g47: LineSegment StartX=0.958792 StartY=0.2 StartZ=0 EndX=1.05 EndY=0.3 EndZ=0
    g48: LineSegment StartX=1.05 StartY=0.3 StartZ=0 EndX=1.05 EndY=0.85 EndZ=0
    g49: ArcOfCircle CenterX=1 CenterY=0.85 CenterZ=0 NormalX=0 NormalY=0 NormalZ=1 AngleXU=0 Radius=0.05 StartAngle=1e-15 EndAngle=1.5708
    g50: LineSegment StartX=1 StartY=0.9 StartZ=0 EndX=0.799491 EndY=0.9 EndZ=0
    g51: LineSegment StartX=0.838792 StartY=0.2 StartZ=0 EndX=0.958792 EndY=0.2 EndZ=0
  constraints (94):
    c: Vertical(g0)
    c: Coincident(g0,g1)
    c: Horizontal(g1)
    c: Coincident(g2,g3)
    c: Vertical(g3)
    c: Coincident(g3,g4)
    c: Coincident(g4,g5)
    c: Horizontal(g5)
    c: Coincident(g5,g6)
    c: Coincident(g6,g7)
    c: Vertical(g7)
    c: Coincident(g7,g8)
    c: Horizontal(g8)
    c: Coincident(g8,g0)
    c: Block(g2)
    c: Block(g0)
    c: Coincident(g2,g9)
    c: Vertical(g9)
    c: Coincident(g1,g9)
    c: Horizontal(g10)
    c: Coincident(g10,g11)
    c: Vertical(g11)
    c: Coincident(g11,g12)
    c: Horizontal(g12)
    c: Coincident(g12,g13)
    c: Vertical(g13)
    c: Coincident(g13,g14)
    c: Coincident(g14,g15)
    c: Horizontal(g15)
    c: Coincident(g15,g16)
    c: Coincident(g16,g17)
    c: Vertical(g17)
    c: Coincident(g17,g18)
    c: Block(g11)
    c: Block(g18)
    c: Vertical(g19)
    c: Coincident(g18,g19)
    c: Coincident(g19,g10)
    c: Coincident(g20,g21)
    c: Vertical(g21)
    c: Coincident(g21,g22)
    c: Coincident(g23,g24)
    c: Vertical(g24)
    c: Coincident(g24,g25)
    c: Coincident(g25,g26)
    c: Horizontal(g26)
    c: Coincident(g26,g20)
    c: Block(g22)
    c: Block(g23)
    c: Coincident(g22,g27)
    c: Coincident(g23,g27)
    c: Horizontal(g27)
    c: Coincident(g28,g29)
    c: Vertical(g29)
    c: Coincident(g29,g30)
    c: Coincident(g31,g32)
    c: Vertical(g32)
    c: Coincident(g32,g33)
    c: Coincident(g33,g34)
    c: Horizontal(g34)
    c: Coincident(g34,g28)
    c: Block(g30)
    c: Block(g31)
    c: Coincident(g30,g35)
    c: Coincident(g31,g35)
    c: Horizontal(g35)
    c: Coincident(g36,g37)
    c: Vertical(g37)
    c: Coincident(g37,g38)
    c: Coincident(g39,g40)
    c: Vertical(g40)
    c: Coincident(g40,g41)
    c: Coincident(g41,g42)
    c: Horizontal(g42)
    c: Coincident(g42,g36)
    c: Block(g38)
    c: Block(g39)
    c: Coincident(g38,g43)
    c: Coincident(g39,g43)
    c: Horizontal(g43)
    c: Coincident(g44,g45)
    c: Vertical(g45)
    c: Coincident(g45,g46)
    c: Coincident(g47,g48)
    c: Vertical(g48)
    c: Coincident(g48,g49)
    c: Coincident(g49,g50)
    c: Horizontal(g50)
    c: Coincident(g50,g44)
    c: Block(g46)
    c: Block(g47)
    c: Coincident(g46,g51)
    c: Coincident(g47,g51)
    c: Horizontal(g51)
FEATURE [Part::Part2DObjectPython] ShapeString  label="Dwgs"  # Draft 2D object (typed FeaturePython)
  FontFile = <userpath>/AppData/Roaming/FreeCAD/Mod/osifont-lgpl3fe.ttf
  MakeFace = true
  Placement = pos=(2.62,0,0) rot=(0,0,1;0rad)
  Size = 1
  String = PLATED
  Tracking = 0
FEATURE [Part::Part2DObjectPython] ShapeString001  label="Cmts"  # Draft 2D object (typed FeaturePython)
  FontFile = <userpath>/AppData/Roaming/FreeCAD/Mod/osifont-lgpl3fe.ttf
  MakeFace = true
  Placement = pos=(2.6185,-1.6055,0) rot=(0,0,1;0rad)
  Size = 1
  String = STIFFENER
  Tracking = 0
FEATURE [Sketcher::SketchObject] Sketch030  label="Dwgs_0.05"
  FullyConstrained = false
  sketch-geometry (138):
    g0: LineSegment StartX=2.82 StartY=0.407383 StartZ=0 EndX=2.82 EndY=0.0590604 EndZ=0
    g1: LineSegment StartX=2.82 StartY=0.0590604 StartZ=0 EndX=2.80611 EndY=0.0202661 EndZ=0
    g2: LineSegment StartX=2.80611 StartY=0.0202661 StartZ=0 EndX=2.77034 EndY=0.0033557 EndZ=0
    g3: LineSegment StartX=2.77034 StartY=0.0033557 StartZ=0 EndX=2.73441 EndY=0.0207837 EndZ=0
    g4: LineSegment StartX=2.73441 StartY=0.0207837 StartZ=0 EndX=2.72067 EndY=0.0604027 EndZ=0
    g5: LineSegment StartX=2.72067 StartY=0.0604027 StartZ=0 EndX=2.72067 EndY=0.960403 EndZ=0
    g6: LineSegment StartX=2.72067 StartY=0.960403 StartZ=0 EndX=2.737 EndY=0.998105 EndZ=0
    g7: LineSegment StartX=2.737 StartY=0.998105 StartZ=0 EndX=2.7757 EndY=1.01342 EndZ=0
    g8: LineSegment StartX=2.7757 StartY=1.01342 StartZ=0 EndX=3.03544 EndY=1.01342 EndZ=0
    g9: LineSegment StartX=3.03544 StartY=1.01342 StartZ=0 EndX=3.15353 EndY=0.986269 EndZ=0
    g10: LineSegment StartX=3.15353 StartY=0.986269 StartZ=0 EndX=3.25087 EndY=0.912752 EndZ=0
    g11: LineSegment StartX=3.25087 StartY=0.912752 StartZ=0 EndX=3.3056 EndY=0.827361 EndZ=0
    g12: LineSegment StartX=3.3056 StartY=0.827361 StartZ=0 EndX=3.32604 EndY=0.728859 EndZ=0
    g13: LineSegment StartX=3.32604 StartY=0.728859 StartZ=0 EndX=3.3152 EndY=0.627774 EndZ=0
    g14: LineSegment StartX=3.3152 StartY=0.627774 StartZ=0 EndX=3.27369 EndY=0.536913 EndZ=0
    g15: LineSegment StartX=3.27369 StartY=0.536913 StartZ=0 EndX=3.17222 EndY=0.444191 EndZ=0
    g16: LineSegment StartX=3.17222 StartY=0.444191 StartZ=0 EndX=3.04282 EndY=0.407383 EndZ=0
    g17: LineSegment StartX=3.04282 StartY=0.407383 StartZ=0 EndX=2.82 EndY=0.407383 EndZ=0
    g18: LineSegment StartX=3.01463 StartY=0.916779 StartZ=0 EndX=2.82 EndY=0.916779 EndZ=0
    g19: LineSegment StartX=2.82 StartY=0.916779 StartZ=0 EndX=2.82 EndY=0.506711 EndZ=0
    g20: LineSegment StartX=2.82 StartY=0.506711 StartZ=0 EndX=3.04282 EndY=0.506711 EndZ=0
    g21: LineSegment StartX=3.04282 StartY=0.506711 StartZ=0 EndX=3.11194 EndY=0.523626 EndZ=0
    g22: LineSegment StartX=3.11194 StartY=0.523626 StartZ=0 EndX=3.17034 EndY=0.566443 EndZ=0
    g23: LineSegment StartX=3.17034 StartY=0.566443 StartZ=0 EndX=3.21436 EndY=0.633592 EndZ=0
    g24: LineSegment StartX=3.21436 StartY=0.633592 StartZ=0 EndX=3.2294 EndY=0.712752 EndZ=0
    g25: LineSegment StartX=3.2294 StartY=0.712752 StartZ=0 EndX=3.21428 EndY=0.791689 EndZ=0
    g26: LineSegment StartX=3.21428 StartY=0.791689 StartZ=0 EndX=3.16998 EndY=0.858389 EndZ=0
    g27: LineSegment StartX=3.16998 StartY=0.858389 StartZ=0 EndX=3.09849 EndY=0.902698 EndZ=0
    g28: LineSegment StartX=3.09849 StartY=0.902698 StartZ=0 EndX=3.01463 EndY=0.916779 EndZ=0
    g29: LineSegment StartX=3.59114 StartY=0.961745 StartZ=0 EndX=3.59114 EndY=0.0973154 EndZ=0
    g30: LineSegment StartX=3.59114 StartY=0.0973154 StartZ=0 EndX=3.94081 EndY=0.0973154 EndZ=0
    g31: LineSegment StartX=3.94081 StartY=0.0973154 StartZ=0 EndX=3.98283 EndY=0.0844643 EndZ=0
    g32: LineSegment StartX=3.98283 StartY=0.0844643 StartZ=0 EndX=4.00188 EndY=0.0486353 EndZ=0
    g33: LineSegment StartX=4.00188 StartY=0.0486353 StartZ=0 EndX=3.98207 EndY=0.0125835 EndZ=0
    g34: LineSegment StartX=3.98207 StartY=0.0125835 StartZ=0 EndX=3.93879 EndY=1e-16 EndZ=0
    g35: LineSegment StartX=3.93879 StartY=0 StartZ=0 EndX=3.54148 EndY=0 EndZ=0
    g36: LineSegment StartX=3.54148 StartY=1e-16 StartZ=0 EndX=3.50641 EndY=0.018626 EndZ=0
    g37: LineSegment StartX=3.50641 StartY=0.018626 StartZ=0 EndX=3.49383 EndY=0.0597315 EndZ=0
    g38: LineSegment StartX=3.49383 StartY=0.0597315 StartZ=0 EndX=3.49383 EndY=0.961745 EndZ=0
    g39: LineSegment StartX=3.49383 StartY=0.961745 StartZ=0 EndX=3.50775 EndY=0.99798 EndZ=0
    g40: LineSegment StartX=3.50775 StartY=0.99798 StartZ=0 EndX=3.54246 EndY=1.01342 EndZ=0
    g41: LineSegment StartX=3.54246 StartY=1.01342 StartZ=0 EndX=3.5772 EndY=0.997984 EndZ=0
    g42: LineSegment StartX=3.5772 StartY=0.997984 StartZ=0 EndX=3.59114 EndY=0.961745 EndZ=0
    g43: LineSegment StartX=4.15083 StartY=0.0973154 StartZ=0 EndX=4.44747 EndY=0.97651 EndZ=0
    g44: LineSegment StartX=4.44747 StartY=0.97651 StartZ=0 EndX=4.46527 EndY=1.00282 EndZ=0
    g45: LineSegment StartX=4.46527 StartY=1.00282 StartZ=0 EndX=4.49445 EndY=1.01342 EndZ=0
    g46: LineSegment StartX=4.49445 StartY=1.01342 StartZ=0 EndX=4.52286 EndY=1.00268 EndZ=0
    g47: LineSegment StartX=4.52286 StartY=1.00268 StartZ=0 EndX=4.54009 EndY=0.97651 EndZ=0
    g48: LineSegment StartX=4.54009 StartY=0.97651 StartZ=0 EndX=4.84009 EndY=0.0744966 EndZ=0
    g49: LineSegment StartX=4.84009 StartY=0.0744966 StartZ=0 EndX=4.84431 EndY=0.0599263 EndZ=0
    g50: LineSegment StartX=4.84431 StartY=0.0599263 StartZ=0 EndX=4.84613 EndY=0.0449664 EndZ=0
    g51: LineSegment StartX=4.84613 StartY=0.0449664 StartZ=0 EndX=4.8314 EndY=0.0140453 EndZ=0
    g52: LineSegment StartX=4.8314 StartY=0.0140453 StartZ=0 EndX=4.79781 EndY=-1e-16 EndZ=0
    g53: LineSegment StartX=4.79781 StartY=2e-16 StartZ=0 EndX=4.76629 EndY=0.0133341 EndZ=0
    g54: LineSegment StartX=4.76629 StartY=0.0133341 StartZ=0 EndX=4.74747 EndY=0.0442953 EndZ=0
    g55: LineSegment StartX=4.74747 StartY=0.0442953 StartZ=0 EndX=4.67902 EndY=0.256376 EndZ=0
    g56: LineSegment StartX=4.67902 StartY=0.256376 StartZ=0 EndX=4.3072 EndY=0.256376 EndZ=0
    g57: LineSegment StartX=4.3072 StartY=0.256376 StartZ=0 EndX=4.23405 EndY=0.0389262 EndZ=0
    g58: LineSegment StartX=4.23405 StartY=0.0389262 StartZ=0 EndX=4.21696 EndY=0.0104269 EndZ=0
    g59: LineSegment StartX=4.21696 StartY=0.0104269 StartZ=0 EndX=4.18841 EndY=-0.00201342 EndZ=0
    g60: LineSegment StartX=4.18841 StartY=-0.00201342 StartZ=0 EndX=4.15173 EndY=0.0119791 EndZ=0
    g61: LineSegment StartX=4.15173 StartY=0.0119791 StartZ=0 EndX=4.13606 EndY=0.0469799 EndZ=0
    g62: LineSegment StartX=4.13606 StartY=0.0469799 StartZ=0 EndX=4.14131 EndY=0.0724987 EndZ=0
    g63: LineSegment StartX=4.14131 StartY=0.0724987 StartZ=0 EndX=4.15083 EndY=0.0973154 EndZ=0
    g64: LineSegment StartX=4.49177 StartY=0.809396 StartZ=0 EndX=4.3374 EndY=0.351007 EndZ=0
    g65: LineSegment StartX=4.3374 StartY=0.351007 StartZ=0 EndX=4.6468 EndY=0.351007 EndZ=0
    g66: LineSegment StartX=4.6468 StartY=0.351007 StartZ=0 EndX=4.49177 EndY=0.809396 EndZ=0
    g67: LineSegment StartX=5.2345 StartY=0.919463 StartZ=0 EndX=5.03852 EndY=0.919463 EndZ=0
    g68: LineSegment StartX=5.03852 StartY=0.919463 StartZ=0 EndX=4.99837 EndY=0.933671 EndZ=0
    g69: LineSegment StartX=4.99837 StartY=0.933671 StartZ=0 EndX=4.98081 EndY=0.97047 EndZ=0
    g70: LineSegment StartX=4.98081 StartY=0.97047 StartZ=0 EndX=4.99929 EndY=1.00467 EndZ=0
    g71: LineSegment StartX=4.99929 StartY=1.00467 StartZ=0 EndX=5.03987 EndY=1.01678 EndZ=0
    g72: LineSegment StartX=5.03987 StartY=1.01678 StartZ=0 EndX=5.53718 EndY=1.01678 EndZ=0
    g73: LineSegment StartX=5.53718 StartY=1.01678 StartZ=0 EndX=5.57135 EndY=1.00263 EndZ=0
    g74: LineSegment StartX=5.57135 StartY=1.00263 StartZ=0 EndX=5.5855 EndY=0.968456 EndZ=0
    g75: LineSegment StartX=5.5855 StartY=0.968456 StartZ=0 EndX=5.57196 EndY=0.934018 EndZ=0
    g76: LineSegment StartX=5.57196 StartY=0.934018 StartZ=0 EndX=5.53852 EndY=0.919463 EndZ=0
    g77: LineSegment StartX=5.53852 StartY=0.919463 StartZ=0 EndX=5.33248 EndY=0.919463 EndZ=0
    g78: LineSegment StartX=5.33248 StartY=0.919463 StartZ=0 EndX=5.33248 EndY=0.0530201 EndZ=0
    g79: LineSegment StartX=5.33248 StartY=0.0530201 StartZ=0 EndX=5.31856 EndY=0.0159322 EndZ=0
    g80: LineSegment StartX=5.31856 StartY=0.0159322 StartZ=0 EndX=5.28349 EndY=1e-16 EndZ=0
    g81: LineSegment StartX=5.28349 StartY=-1e-16 StartZ=0 EndX=5.24856 EndY=0.0154078 EndZ=0
    g82: LineSegment StartX=5.24856 StartY=0.0154078 StartZ=0 EndX=5.2345 EndY=0.0516779 EndZ=0
    g83: LineSegment StartX=5.2345 StartY=0.0516779 StartZ=0 EndX=5.2345 EndY=0.919463 EndZ=0
    g84: LineSegment StartX=5.8498 StartY=0.1 StartZ=0 EndX=6.20752 EndY=0.1 EndZ=0
    g85: LineSegment StartX=6.20752 StartY=0.1 StartZ=0 EndX=6.2425 EndY=0.0859874 EndZ=0
    g86: LineSegment StartX=6.2425 StartY=0.0859874 StartZ=0 EndX=6.25718 EndY=0.0516779 EndZ=0
    g87: LineSegment StartX=6.25718 StartY=0.0516779 StartZ=0 EndX=6.24329 EndY=0.017578 EndZ=0
    g88: LineSegment StartX=6.24329 StartY=0.017578 StartZ=0 EndX=6.20953 EndY=0.0033557 EndZ=0
    g89: LineSegment StartX=6.20953 StartY=0.0033557 StartZ=0 EndX=5.79745 EndY=0.0033557 EndZ=0
    g90: LineSegment StartX=5.79745 StartY=0.0033557 StartZ=0 EndX=5.76547 EndY=0.0186901 EndZ=0
    g91: LineSegment StartX=5.76547 StartY=0.0186901 StartZ=0 EndX=5.75315 EndY=0.0536913 EndZ=0
    g92: LineSegment StartX=5.75315 StartY=0.0536913 StartZ=0 EndX=5.75315 EndY=0.96443 EndZ=0
    g93: LineSegment StartX=5.75315 StartY=0.96443 StartZ=0 EndX=5.77137 EndY=1.00225 EndZ=0
    g94: LineSegment StartX=5.77137 StartY=1.00225 StartZ=0 EndX=5.81289 EndY=1.01678 EndZ=0
    g95: LineSegment StartX=5.81289 StartY=1.01678 StartZ=0 EndX=6.20416 EndY=1.01678 EndZ=0
    g96: LineSegment StartX=6.20416 StartY=1.01678 StartZ=0 EndX=6.24207 EndY=1.00301 EndZ=0
    g97: LineSegment StartX=6.24207 StartY=1.00301 StartZ=0 EndX=6.25852 EndY=0.967785 EndZ=0
    g98: LineSegment StartX=6.25852 StartY=0.967785 StartZ=0 EndX=6.24201 EndY=0.932959 EndZ=0
    g99: LineSegment StartX=6.24201 StartY=0.932959 StartZ=0 EndX=6.20416 EndY=0.919463 EndZ=0
    g100: LineSegment StartX=6.20416 StartY=0.919463 StartZ=0 EndX=5.8498 EndY=0.919463 EndZ=0
    g101: LineSegment StartX=5.8498 StartY=0.919463 StartZ=0 EndX=5.8498 EndY=0.606711 EndZ=0
    g102: LineSegment StartX=5.8498 StartY=0.606711 StartZ=0 EndX=6.10886 EndY=0.606711 EndZ=0
    g103: LineSegment StartX=6.10886 StartY=0.606711 StartZ=0 EndX=6.14343 EndY=0.592628 EndZ=0
    g104: LineSegment StartX=6.14343 StartY=0.592628 StartZ=0 EndX=6.15785 EndY=0.558389 EndZ=0
    g105: LineSegment StartX=6.15785 StartY=0.558389 StartZ=0 EndX=6.14369 EndY=0.525906 EndZ=0
    g106: LineSegment StartX=6.14369 StartY=0.525906 StartZ=0 EndX=6.1102 EndY=0.512752 EndZ=0
    g107: LineSegment StartX=6.1102 StartY=0.512752 StartZ=0 EndX=5.8498 EndY=0.512752 EndZ=0
    g108: LineSegment StartX=5.8498 StartY=0.512752 StartZ=0 EndX=5.8498 EndY=0.1 EndZ=0
    g109: LineSegment StartX=6.42609 StartY=0.0597315 StartZ=0 EndX=6.42609 EndY=0.958389 EndZ=0
    g110: LineSegment StartX=6.42609 StartY=0.958389 StartZ=0 EndX=6.44247 EndY=0.997374 EndZ=0
    g111: LineSegment StartX=6.44247 StartY=0.997374 StartZ=0 EndX=6.48179 EndY=1.01342 EndZ=0
    g112: LineSegment StartX=6.48179 StartY=1.01342 StartZ=0 EndX=6.79655 EndY=1.01342 EndZ=0
    g113: LineSegment StartX=6.79655 StartY=1.01342 StartZ=0 EndX=6.88582 EndY=0.993767 EndZ=0
    g114: LineSegment StartX=6.88582 StartY=0.993767 StartZ=0 EndX=6.9613 EndY=0.94094 EndZ=0
    g115: LineSegment StartX=6.9613 StartY=0.94094 StartZ=0 EndX=7.01385 EndY=0.865524 EndZ=0
    g116: LineSegment StartX=7.01385 StartY=0.865524 StartZ=0 EndX=7.03347 EndY=0.77651 EndZ=0
    g117: LineSegment StartX=7.03347 StartY=0.77651 StartZ=0 EndX=7.03347 EndY=0.234899 EndZ=0
    g118: LineSegment StartX=7.03347 StartY=0.234899 StartZ=0 EndX=7.01378 EndY=0.146253 EndZ=0
    g119: LineSegment StartX=7.01378 StartY=0.146253 StartZ=0 EndX=6.96098 EndY=0.0714541 EndZ=0
    g120: LineSegment StartX=6.96098 StartY=0.0714541 StartZ=0 EndX=6.88985 EndY=0.0201519 EndZ=0
    g121: LineSegment StartX=6.88985 StartY=0.0201519 StartZ=0 EndX=6.80595 EndY=0 EndZ=0
    g122: LineSegment StartX=6.80595 StartY=0 StartZ=0 EndX=6.47105 EndY=0 EndZ=0
    g123: LineSegment StartX=6.47105 StartY=0 StartZ=0 EndX=6.43754 EndY=0.0188403 EndZ=0
    g124: LineSegment StartX=6.43754 StartY=0.0188403 StartZ=0 EndX=6.42609 EndY=0.0597315 EndZ=0
    g125: LineSegment StartX=6.77776 StartY=0.916779 StartZ=0 EndX=6.52474 EndY=0.916779 EndZ=0
    g126: LineSegment StartX=6.52474 StartY=0.916779 StartZ=0 EndX=6.52474 EndY=0.0966443 EndZ=0
    g127: LineSegment StartX=6.52474 StartY=0.0966443 StartZ=0 EndX=6.52475 EndY=0.095782 EndZ=0
    g128: LineSegment StartX=6.52475 StartY=0.095782 StartZ=0 EndX=6.75763 EndY=0.0966443 EndZ=0
    g129: LineSegment StartX=6.75763 StartY=0.0966443 StartZ=0 EndX=6.83064 EndY=0.106526 EndZ=0
    g130: LineSegment StartX=6.83064 StartY=0.106526 StartZ=0 EndX=6.89217 EndY=0.143266 EndZ=0
    g131: LineSegment StartX=6.89217 StartY=0.143266 StartZ=0 EndX=6.92551 EndY=0.196072 EndZ=0
    g132: LineSegment StartX=6.92551 StartY=0.196072 StartZ=0 EndX=6.93682 EndY=0.257718 EndZ=0
    g133: LineSegment StartX=6.93682 StartY=0.257718 StartZ=0 EndX=6.93682 EndY=0.761745 EndZ=0
    g134: LineSegment StartX=6.93682 StartY=0.761745 StartZ=0 EndX=6.92514 EndY=0.819372 EndZ=0
    g135: LineSegment StartX=6.92514 StartY=0.819372 StartZ=0 EndX=6.8932 EndY=0.869128 EndZ=0
    g136: LineSegment StartX=6.8932 StartY=0.869128 StartZ=0 EndX=6.84078 EndY=0.90498 EndZ=0
    g137: LineSegment StartX=6.84078 StartY=0.90498 StartZ=0 EndX=6.77776 EndY=0.916779 EndZ=0
FEATURE [Sketcher::SketchObject] Sketch031  label="Cmts_0.05"
  FullyConstrained = false
  sketch-geometry (225):
    g0: LineSegment StartX=3.09233 StartY=-1.20416 StartZ=0 EndX=2.82857 EndY=-1.0706 EndZ=0
    g1: LineSegment StartX=2.82857 StartY=-1.0706 StartZ=0 EndX=2.72508 EndY=-0.97818 EndZ=0
    g2: LineSegment StartX=2.72508 StartY=-0.97818 StartZ=0 EndX=2.68561 EndY=-0.84644 EndZ=0
    g3: LineSegment StartX=2.68561 StartY=-0.84644 StartZ=0 EndX=2.70438 EndY=-0.749607 EndZ=0
    g4: LineSegment StartX=2.70438 StartY=-0.749607 StartZ=0 EndX=2.7581 EndY=-0.666932 EndZ=0
    g5: LineSegment StartX=2.7581 StartY=-0.666932 StartZ=0 EndX=2.83813 EndY=-0.611693 EndZ=0
    g6: LineSegment StartX=2.83813 StartY=-0.611693 StartZ=0 EndX=2.93327 EndY=-0.592077 EndZ=0
    g7: LineSegment StartX=2.93327 StartY=-0.592077 StartZ=0 EndX=3.06457 EndY=-0.602274 EndZ=0
    g8: LineSegment StartX=3.06457 StartY=-0.602274 StartZ=0 EndX=3.19165 EndY=-0.635701 EndZ=0
    g9: LineSegment StartX=3.19165 StartY=-0.635701 StartZ=0 EndX=3.22534 EndY=-0.656956 EndZ=0
    g10: LineSegment StartX=3.22534 StartY=-0.656956 StartZ=0 EndX=3.23998 EndY=-0.691406 EndZ=0
    g11: LineSegment StartX=3.23998 StartY=-0.691406 StartZ=0 EndX=3.22641 EndY=-0.724151 EndZ=0
    g12: LineSegment StartX=3.22641 StartY=-0.724151 StartZ=0 EndX=3.19367 EndY=-0.737715 EndZ=0
    g13: LineSegment StartX=3.19367 StartY=-0.737715 StartZ=0 EndX=3.16259 EndY=-0.732543 EndZ=0
    g14: LineSegment StartX=3.16259 StartY=-0.732543 StartZ=0 EndX=3.13259 EndY=-0.721607 EndZ=0
    g15: LineSegment StartX=3.13259 StartY=-0.721607 StartZ=0 EndX=3.04191 EndY=-0.696282 EndZ=0
    g16: LineSegment StartX=3.04191 StartY=-0.696282 StartZ=0 EndX=2.94803 EndY=-0.68805 EndZ=0
    g17: LineSegment StartX=2.94803 StartY=-0.68805 StartZ=0 EndX=2.87254 EndY=-0.703725 EndZ=0
    g18: LineSegment StartX=2.87254 StartY=-0.703725 StartZ=0 EndX=2.81313 EndY=-0.751138 EndZ=0
    g19: LineSegment StartX=2.81313 StartY=-0.751138 StartZ=0 EndX=2.79108 EndY=-0.798858 EndZ=0
    g20: LineSegment StartX=2.79108 StartY=-0.798858 StartZ=0 EndX=2.78494 EndY=-0.851809 EndZ=0
    g21: LineSegment StartX=2.78494 StartY=-0.851809 StartZ=0 EndX=2.81607 EndY=-0.933731 EndZ=0
    g22: LineSegment StartX=2.81607 StartY=-0.933731 StartZ=0 EndX=2.88897 EndY=-0.990064 EndZ=0
    g23: LineSegment StartX=2.88897 StartY=-0.990064 StartZ=0 EndX=3.13394 EndY=-1.11422 EndZ=0
    g24: LineSegment StartX=3.13394 StartY=-1.11422 StartZ=0 EndX=3.24778 EndY=-1.21209 EndZ=0
    g25: LineSegment StartX=3.24778 StartY=-1.21209 StartZ=0 EndX=3.293 EndY=-1.35181 EndZ=0
    g26: LineSegment StartX=3.293 StartY=-1.35181 StartZ=0 EndX=3.27182 EndY=-1.45546 EndZ=0
    g27: LineSegment StartX=3.27182 StartY=-1.45546 StartZ=0 EndX=3.20978 EndY=-1.5404 EndZ=0
    g28: LineSegment StartX=3.20978 StartY=-1.5404 StartZ=0 EndX=3.12555 EndY=-1.58917 EndZ=0
    g29: LineSegment StartX=3.12555 StartY=-1.58917 StartZ=0 EndX=3.02924 EndY=-1.6055 EndZ=0
    g30: LineSegment StartX=3.02924 StartY=-1.6055 StartZ=0 EndX=2.86951 EndY=-1.57998 EndZ=0
    g31: LineSegment StartX=2.86951 StartY=-1.57998 StartZ=0 EndX=2.7232 EndY=-1.50953 EndZ=0
    g32: LineSegment StartX=2.7232 StartY=-1.50953 StartZ=0 EndX=2.69698 EndY=-1.48601 EndZ=0
    g33: LineSegment StartX=2.69698 StartY=-1.48601 StartZ=0 EndX=2.68561 EndY=-1.45449 EndZ=0
    g34: LineSegment StartX=2.68561 StartY=-1.45449 StartZ=0 EndX=2.7005 EndY=-1.42139 EndZ=0
    g35: LineSegment StartX=2.7005 StartY=-1.42139 StartZ=0 EndX=2.73528 EndY=-1.40818 EndZ=0
    g36: LineSegment StartX=2.73528 StartY=-1.40818 StartZ=0 EndX=2.7607 EndY=-1.41498 EndZ=0
    g37: LineSegment StartX=2.7607 StartY=-1.41498 StartZ=0 EndX=2.7836 EndY=-1.42966 EndZ=0
    g38: LineSegment StartX=2.7836 StartY=-1.42966 StartZ=0 EndX=2.90444 EndY=-1.48736 EndZ=0
    g39: LineSegment StartX=2.90444 StartY=-1.48736 StartZ=0 EndX=3.03796 EndY=-1.5055 EndZ=0
    g40: LineSegment StartX=3.03796 StartY=-1.5055 StartZ=0 EndX=3.07837 EndY=-1.50115 EndZ=0
    g41: LineSegment StartX=3.07837 StartY=-1.50115 StartZ=0 EndX=3.11649 EndY=-1.48738 EndZ=0
    g42: LineSegment StartX=3.11649 StartY=-1.48738 StartZ=0 EndX=3.17408 EndY=-1.42943 EndZ=0
    g43: LineSegment StartX=3.17408 StartY=-1.42943 StartZ=0 EndX=3.19367 EndY=-1.34845 EndZ=0
    g44: LineSegment StartX=3.19367 StartY=-1.34845 StartZ=0 EndX=3.1643 EndY=-1.26318 EndZ=0
    g45: LineSegment StartX=3.1643 StartY=-1.26318 StartZ=0 EndX=3.09233 EndY=-1.20416 EndZ=0
    g46: LineSegment StartX=3.68096 StartY=-0.686037 StartZ=0 EndX=3.48499 EndY=-0.686037 EndZ=0
    g47: LineSegment StartX=3.48499 StartY=-0.686037 StartZ=0 EndX=3.44483 EndY=-0.671829 EndZ=0
    g48: LineSegment StartX=3.44483 StartY=-0.671829 StartZ=0 EndX=3.42727 EndY=-0.63503 EndZ=0
    g49: LineSegment StartX=3.42727 StartY=-0.63503 StartZ=0 EndX=3.44575 EndY=-0.600828 EndZ=0
    g50: LineSegment StartX=3.44575 StartY=-0.600828 StartZ=0 EndX=3.48633 EndY=-0.588721 EndZ=0
    g51: LineSegment StartX=3.48633 StartY=-0.588721 StartZ=0 EndX=3.98365 EndY=-0.588721 EndZ=0
    g52: LineSegment StartX=3.98365 StartY=-0.588721 StartZ=0 EndX=4.01781 EndY=-0.602875 EndZ=0
    g53: LineSegment StartX=4.01781 StartY=-0.602875 StartZ=0 EndX=4.03197 EndY=-0.637044 EndZ=0
    g54: LineSegment StartX=4.03197 StartY=-0.637044 StartZ=0 EndX=4.01842 EndY=-0.671482 EndZ=0
    g55: LineSegment StartX=4.01842 StartY=-0.671482 StartZ=0 EndX=3.98499 EndY=-0.686037 EndZ=0
    g56: LineSegment StartX=3.98499 StartY=-0.686037 StartZ=0 EndX=3.77895 EndY=-0.686037 EndZ=0
    g57: LineSegment StartX=3.77895 StartY=-0.686037 StartZ=0 EndX=3.77895 EndY=-1.55248 EndZ=0
    g58: LineSegment StartX=3.77895 StartY=-1.55248 StartZ=0 EndX=3.76503 EndY=-1.58957 EndZ=0
    g59: LineSegment StartX=3.76503 StartY=-1.58957 StartZ=0 EndX=3.72995 EndY=-1.6055 EndZ=0
    g60: LineSegment StartX=3.72995 StartY=-1.6055 StartZ=0 EndX=3.69503 EndY=-1.59009 EndZ=0
    g61: LineSegment StartX=3.69503 StartY=-1.59009 StartZ=0 EndX=3.68096 EndY=-1.55382 EndZ=0
    g62: LineSegment StartX=3.68096 StartY=-1.55382 StartZ=0 EndX=3.68096 EndY=-0.686037 EndZ=0
    g63: LineSegment StartX=4.30163 StartY=-0.654493 StartZ=0 EndX=4.30163 EndY=-1.54107 EndZ=0
    g64: LineSegment StartX=4.30163 StartY=-1.54107 StartZ=0 EndX=4.28822 EndY=-1.58538 EndZ=0
    g65: LineSegment StartX=4.28822 StartY=-1.58538 StartZ=0 EndX=4.25063 EndY=-1.6055 EndZ=0
    g66: LineSegment StartX=4.25063 StartY=-1.6055 StartZ=0 EndX=4.21319 EndY=-1.58588 EndZ=0
    g67: LineSegment StartX=4.21319 StartY=-1.58588 StartZ=0 EndX=4.19962 EndY=-1.54241 EndZ=0
    g68: LineSegment StartX=4.19962 StartY=-1.54241 StartZ=0 EndX=4.19962 EndY=-0.65248 EndZ=0
    g69: LineSegment StartX=4.19962 StartY=-0.65248 StartZ=0 EndX=4.21352 EndY=-0.610672 EndZ=0
    g70: LineSegment StartX=4.21352 StartY=-0.610672 StartZ=0 EndX=4.25063 EndY=-0.592077 EndZ=0
    g71: LineSegment StartX=4.25063 StartY=-0.592077 StartZ=0 EndX=4.28798 EndY=-0.611439 EndZ=0
    g72: LineSegment StartX=4.28798 StartY=-0.611439 StartZ=0 EndX=4.30163 EndY=-0.654493 EndZ=0
    g73: LineSegment StartX=4.60248 StartY=-1.09342 StartZ=0 EndX=4.60248 EndY=-1.54778 EndZ=0
    g74: LineSegment StartX=4.60248 StartY=-1.54778 StartZ=0 EndX=4.58824 EndY=-1.58623 EndZ=0
    g75: LineSegment StartX=4.58824 StartY=-1.58623 StartZ=0 EndX=4.55215 EndY=-1.60282 EndZ=0
    g76: LineSegment StartX=4.55215 StartY=-1.60282 StartZ=0 EndX=4.51677 EndY=-1.58584 EndZ=0
    g77: LineSegment StartX=4.51677 StartY=-1.58584 StartZ=0 EndX=4.50315 EndY=-1.54711 EndZ=0
    g78: LineSegment StartX=4.50315 StartY=-1.54711 StartZ=0 EndX=4.50315 EndY=-0.635701 EndZ=0
    g79: LineSegment StartX=4.50315 StartY=-0.635701 StartZ=0 EndX=4.51902 EndY=-0.6019 EndZ=0
    g80: LineSegment StartX=4.51902 StartY=-0.6019 StartZ=0 EndX=4.5555 EndY=-0.588721 EndZ=0
    g81: LineSegment StartX=4.5555 StartY=-0.588721 StartZ=0 EndX=4.9555 EndY=-0.588721 EndZ=0
    g82: LineSegment StartX=4.9555 StartY=-0.588721 StartZ=0 EndX=4.99253 EndY=-0.602369 EndZ=0
    g83: LineSegment StartX=4.99253 StartY=-0.602369 StartZ=0 EndX=5.00852 EndY=-0.637044 EndZ=0
    g84: LineSegment StartX=5.00852 StartY=-0.637044 StartZ=0 EndX=4.99279 EndY=-0.671644 EndZ=0
    g85: LineSegment StartX=4.99279 StartY=-0.671644 StartZ=0 EndX=4.95617 EndY=-0.685366 EndZ=0
    g86: LineSegment StartX=4.95617 StartY=-0.685366 StartZ=0 EndX=4.60315 EndY=-0.685366 EndZ=0
    g87: LineSegment StartX=4.60315 StartY=-0.685366 StartZ=0 EndX=4.60315 EndY=-0.995433 EndZ=0
    g88: LineSegment StartX=4.60315 StartY=-0.995433 StartZ=0 EndX=4.95617 EndY=-0.995433 EndZ=0
    g89: LineSegment StartX=4.95617 StartY=-0.995433 StartZ=0 EndX=4.99285 EndY=-1.00943 EndZ=0
    g90: LineSegment StartX=4.99285 StartY=-1.00943 StartZ=0 EndX=5.00852 EndY=-1.04443 EndZ=0
    g91: LineSegment StartX=5.00852 StartY=-1.04443 StartZ=0 EndX=4.99259 EndY=-1.0795 EndZ=0
    g92: LineSegment StartX=4.99259 StartY=-1.0795 StartZ=0 EndX=4.9555 EndY=-1.09342 EndZ=0
    g93: LineSegment StartX=4.9555 StartY=-1.09342 StartZ=0 EndX=4.60248 EndY=-1.09342 EndZ=0
    g94: LineSegment StartX=5.27541 StartY=-1.09342 StartZ=0 EndX=5.27541 EndY=-1.54778 EndZ=0
    g95: LineSegment StartX=5.27541 StartY=-1.54778 StartZ=0 EndX=5.26117 EndY=-1.58623 EndZ=0
    g96: LineSegment StartX=5.26117 StartY=-1.58623 StartZ=0 EndX=5.22508 EndY=-1.60282 EndZ=0
    g97: LineSegment StartX=5.22508 StartY=-1.60282 StartZ=0 EndX=5.1897 EndY=-1.58584 EndZ=0
    g98: LineSegment StartX=5.1897 StartY=-1.58584 StartZ=0 EndX=5.17608 EndY=-1.54711 EndZ=0
    g99: LineSegment StartX=5.17608 StartY=-1.54711 StartZ=0 EndX=5.17608 EndY=-0.635701 EndZ=0
    g100: LineSegment StartX=5.17608 StartY=-0.635701 StartZ=0 EndX=5.19195 EndY=-0.6019 EndZ=0
    g101: LineSegment StartX=5.19195 StartY=-0.6019 StartZ=0 EndX=5.22843 EndY=-0.588721 EndZ=0
    g102: LineSegment StartX=5.22843 StartY=-0.588721 StartZ=0 EndX=5.62843 EndY=-0.588721 EndZ=0
    g103: LineSegment StartX=5.62843 StartY=-0.588721 StartZ=0 EndX=5.66546 EndY=-0.602369 EndZ=0
    g104: LineSegment StartX=5.66546 StartY=-0.602369 StartZ=0 EndX=5.68145 EndY=-0.637044 EndZ=0
    g105: LineSegment StartX=5.68145 StartY=-0.637044 StartZ=0 EndX=5.66572 EndY=-0.671644 EndZ=0
    g106: LineSegment StartX=5.66572 StartY=-0.671644 StartZ=0 EndX=5.6291 EndY=-0.685366 EndZ=0
    g107: LineSegment StartX=5.6291 StartY=-0.685366 StartZ=0 EndX=5.27608 EndY=-0.685366 EndZ=0
    g108: LineSegment StartX=5.27608 StartY=-0.685366 StartZ=0 EndX=5.27608 EndY=-0.995433 EndZ=0
    g109: LineSegment StartX=5.27608 StartY=-0.995433 StartZ=0 EndX=5.6291 EndY=-0.995433 EndZ=0
    g110: LineSegment StartX=5.6291 StartY=-0.995433 StartZ=0 EndX=5.66578 EndY=-1.00943 EndZ=0
    g111: LineSegment StartX=5.66578 StartY=-1.00943 StartZ=0 EndX=5.68145 EndY=-1.04443 EndZ=0
    g112: LineSegment StartX=5.68145 StartY=-1.04443 StartZ=0 EndX=5.66552 EndY=-1.0795 EndZ=0
    g113: LineSegment StartX=5.66552 StartY=-1.0795 StartZ=0 EndX=5.62843 EndY=-1.09342 EndZ=0
    g114: LineSegment StartX=5.62843 StartY=-1.09342 StartZ=0 EndX=5.27541 EndY=-1.09342 EndZ=0
    g115: LineSegment StartX=5.94566 StartY=-1.5055 StartZ=0 EndX=6.30338 EndY=-1.5055 EndZ=0
    g116: LineSegment StartX=6.30338 StartY=-1.5055 StartZ=0 EndX=6.33836 EndY=-1.51951 EndZ=0
    g117: LineSegment StartX=6.33836 StartY=-1.51951 StartZ=0 EndX=6.35304 EndY=-1.55382 EndZ=0
    g118: LineSegment StartX=6.35304 StartY=-1.55382 StartZ=0 EndX=6.33915 EndY=-1.58792 EndZ=0
    g119: LineSegment StartX=6.33915 StartY=-1.58792 StartZ=0 EndX=6.30539 EndY=-1.60214 EndZ=0
    g120: LineSegment StartX=6.30539 StartY=-1.60214 StartZ=0 EndX=5.89331 EndY=-1.60214 EndZ=0
    g121: LineSegment StartX=5.89331 StartY=-1.60214 StartZ=0 EndX=5.86133 EndY=-1.58681 EndZ=0
    g122: LineSegment StartX=5.86133 StartY=-1.58681 StartZ=0 EndX=5.84901 EndY=-1.55181 EndZ=0
    g123: LineSegment StartX=5.84901 StartY=-1.55181 StartZ=0 EndX=5.84901 EndY=-0.64107 EndZ=0
    g124: LineSegment StartX=5.84901 StartY=-0.64107 StartZ=0 EndX=5.86723 EndY=-0.603247 EndZ=0
    g125: LineSegment StartX=5.86723 StartY=-0.603247 StartZ=0 EndX=5.90875 EndY=-0.588721 EndZ=0
    g126: LineSegment StartX=5.90875 StartY=-0.588721 StartZ=0 EndX=6.30002 EndY=-0.588721 EndZ=0
    g127: LineSegment StartX=6.30002 StartY=-0.588721 StartZ=0 EndX=6.33793 EndY=-0.602491 EndZ=0
    g128: LineSegment StartX=6.33793 StartY=-0.602491 StartZ=0 EndX=6.35438 EndY=-0.637715 EndZ=0
    g129: LineSegment StartX=6.35438 StartY=-0.637715 StartZ=0 EndX=6.33787 EndY=-0.672541 EndZ=0
    g130: LineSegment StartX=6.33787 StartY=-0.672541 StartZ=0 EndX=6.30002 EndY=-0.686037 EndZ=0
    g131: LineSegment StartX=6.30002 StartY=-0.686037 StartZ=0 EndX=5.94566 EndY=-0.686037 EndZ=0
    g132: LineSegment StartX=5.94566 StartY=-0.686037 StartZ=0 EndX=5.94566 EndY=-0.998789 EndZ=0
    g133: LineSegment StartX=5.94566 StartY=-0.998789 StartZ=0 EndX=6.20472 EndY=-0.998789 EndZ=0
    g134: LineSegment StartX=6.20472 StartY=-0.998789 StartZ=0 EndX=6.23929 EndY=-1.01287 EndZ=0
    g135: LineSegment StartX=6.23929 StartY=-1.01287 StartZ=0 EndX=6.25371 EndY=-1.04711 EndZ=0
    g136: LineSegment StartX=6.25371 StartY=-1.04711 StartZ=0 EndX=6.23955 EndY=-1.07959 EndZ=0
    g137: LineSegment StartX=6.23955 StartY=-1.07959 StartZ=0 EndX=6.20606 EndY=-1.09275 EndZ=0
    g138: LineSegment StartX=6.20606 StartY=-1.09275 StartZ=0 EndX=5.94566 EndY=-1.09275 EndZ=0
    g139: LineSegment StartX=5.94566 StartY=-1.09275 StartZ=0 EndX=5.94566 EndY=-1.5055 EndZ=0
    g140: LineSegment StartX=7.0347 StartY=-1.3659 StartZ=0 EndX=7.0347 EndY=-0.639728 EndZ=0
    g141: LineSegment StartX=7.0347 StartY=-0.639728 StartZ=0 EndX=7.04775 EndY=-0.604127 EndZ=0
    g142: LineSegment StartX=7.04775 StartY=-0.604127 StartZ=0 EndX=7.08101 EndY=-0.588721 EndZ=0
    g143: LineSegment StartX=7.08101 StartY=-0.588721 StartZ=0 EndX=7.11404 EndY=-0.603343 EndZ=0
    g144: LineSegment StartX=7.11404 StartY=-0.603343 StartZ=0 EndX=7.12731 EndY=-0.637715 EndZ=0
    g145: LineSegment StartX=7.12731 StartY=-0.637715 StartZ=0 EndX=7.12731 EndY=-1.54577 EndZ=0
    g146: LineSegment StartX=7.12731 StartY=-1.54577 StartZ=0 EndX=7.11564 EndY=-1.58409 EndZ=0
    g147: LineSegment StartX=7.11564 StartY=-1.58409 StartZ=0 EndX=7.08302 EndY=-1.60147 EndZ=0
    g148: LineSegment StartX=7.08302 StartY=-1.60147 StartZ=0 EndX=7.05318 EndY=-1.59072 EndZ=0
    g149: LineSegment StartX=7.05318 StartY=-1.59072 StartZ=0 EndX=7.03201 EndY=-1.56523 EndZ=0
    g150: LineSegment StartX=7.03201 StartY=-1.56523 StartZ=0 EndX=6.61859 EndY=-0.827648 EndZ=0
    g151: LineSegment StartX=6.61859 StartY=-0.827648 StartZ=0 EndX=6.61859 EndY=-1.54577 EndZ=0
    g152: LineSegment StartX=6.61859 StartY=-1.54577 StartZ=0 EndX=6.60393 EndY=-1.58346 EndZ=0
    g153: LineSegment StartX=6.60393 StartY=-1.58346 StartZ=0 EndX=6.56758 EndY=-1.59946 EndZ=0
    g154: LineSegment StartX=6.56758 StartY=-1.59946 StartZ=0 EndX=6.53426 EndY=-1.58245 EndZ=0
    g155: LineSegment StartX=6.53426 StartY=-1.58245 StartZ=0 EndX=6.52195 EndY=-1.54443 EndZ=0
    g156: LineSegment StartX=6.52195 StartY=-1.54443 StartZ=0 EndX=6.52195 EndY=-0.648453 EndZ=0
    g157: LineSegment StartX=6.52195 StartY=-0.648453 StartZ=0 EndX=6.53481 EndY=-0.607292 EndZ=0
    g158: LineSegment StartX=6.53481 StartY=-0.607292 StartZ=0 EndX=6.57027 EndY=-0.588721 EndZ=0
    g159: LineSegment StartX=6.57027 StartY=-0.588721 StartZ=0 EndX=6.59871 EndY=-0.597392 EndZ=0
    g160: LineSegment StartX=6.59871 StartY=-0.597392 StartZ=0 EndX=6.61926 EndY=-0.619594 EndZ=0
    g161: LineSegment StartX=6.61926 StartY=-0.619594 StartZ=0 EndX=7.0347 EndY=-1.3659 EndZ=0
    g162: LineSegment StartX=7.42611 StartY=-1.5055 StartZ=0 EndX=7.78382 EndY=-1.5055 EndZ=0
    g163: LineSegment StartX=7.78382 StartY=-1.5055 StartZ=0 EndX=7.81881 EndY=-1.51951 EndZ=0
    g164: LineSegment StartX=7.81881 StartY=-1.51951 StartZ=0 EndX=7.83349 EndY=-1.55382 EndZ=0
    g165: LineSegment StartX=7.83349 StartY=-1.55382 StartZ=0 EndX=7.8196 EndY=-1.58792 EndZ=0
    g166: LineSegment StartX=7.8196 StartY=-1.58792 StartZ=0 EndX=7.78584 EndY=-1.60214 EndZ=0
    g167: LineSegment StartX=7.78584 StartY=-1.60214 StartZ=0 EndX=7.37376 EndY=-1.60214 EndZ=0
    g168: LineSegment StartX=7.37376 StartY=-1.60214 StartZ=0 EndX=7.34178 EndY=-1.58681 EndZ=0
    g169: LineSegment StartX=7.34178 StartY=-1.58681 StartZ=0 EndX=7.32946 EndY=-1.55181 EndZ=0
    g170: LineSegment StartX=7.32946 StartY=-1.55181 StartZ=0 EndX=7.32946 EndY=-0.64107 EndZ=0
    g171: LineSegment StartX=7.32946 StartY=-0.64107 StartZ=0 EndX=7.34768 EndY=-0.603247 EndZ=0
    g172: LineSegment StartX=7.34768 StartY=-0.603247 StartZ=0 EndX=7.38919 EndY=-0.588721 EndZ=0
    g173: LineSegment StartX=7.38919 StartY=-0.588721 StartZ=0 EndX=7.78047 EndY=-0.588721 EndZ=0
    g174: LineSegment StartX=7.78047 StartY=-0.588721 StartZ=0 EndX=7.81838 EndY=-0.602491 EndZ=0
    g175: LineSegment StartX=7.81838 StartY=-0.602491 StartZ=0 EndX=7.83483 EndY=-0.637715 EndZ=0
    g176: LineSegment StartX=7.83483 StartY=-0.637715 StartZ=0 EndX=7.81831 EndY=-0.672541 EndZ=0
    g177: LineSegment StartX=7.81831 StartY=-0.672541 StartZ=0 EndX=7.78047 EndY=-0.686037 EndZ=0
    g178: LineSegment StartX=7.78047 StartY=-0.686037 StartZ=0 EndX=7.42611 EndY=-0.686037 EndZ=0
    g179: LineSegment StartX=7.42611 StartY=-0.686037 StartZ=0 EndX=7.42611 EndY=-0.998789 EndZ=0
    g180: LineSegment StartX=7.42611 StartY=-0.998789 StartZ=0 EndX=7.68517 EndY=-0.998789 EndZ=0
    g181: LineSegment StartX=7.68517 StartY=-0.998789 StartZ=0 EndX=7.71974 EndY=-1.01287 EndZ=0
    g182: LineSegment StartX=7.71974 StartY=-1.01287 StartZ=0 EndX=7.73416 EndY=-1.04711 EndZ=0
    g183: LineSegment StartX=7.73416 StartY=-1.04711 StartZ=0 EndX=7.72 EndY=-1.07959 EndZ=0
    g184: LineSegment StartX=7.72 StartY=-1.07959 StartZ=0 EndX=7.68651 EndY=-1.09275 EndZ=0
    g185: LineSegment StartX=7.68651 StartY=-1.09275 StartZ=0 EndX=7.42611 EndY=-1.09275 EndZ=0
    g186: LineSegment StartX=7.42611 StartY=-1.09275 StartZ=0 EndX=7.42611 EndY=-1.5055 EndZ=0
    g187: LineSegment StartX=8.05474 StartY=-0.596104 StartZ=0 EndX=8.31984 EndY=-0.596104 EndZ=0
    g188: LineSegment StartX=8.31984 StartY=-0.596104 StartZ=0 EndX=8.44217 EndY=-0.627121 EndZ=0
    g189: LineSegment StartX=8.44217 StartY=-0.627121 StartZ=0 EndX=8.54333 EndY=-0.706171 EndZ=0
    g190: LineSegment StartX=8.54333 StartY=-0.706171 StartZ=0 EndX=8.59217 EndY=-0.782982 EndZ=0
    g191: LineSegment StartX=8.59217 StartY=-0.782982 StartZ=0 EndX=8.60978 EndY=-0.871943 EndZ=0
    g192: LineSegment StartX=8.60978 StartY=-0.871943 StartZ=0 EndX=8.60149 EndY=-0.958232 EndZ=0
    g193: LineSegment StartX=8.60149 StartY=-0.958232 StartZ=0 EndX=8.57622 EndY=-1.04107 EndZ=0
    g194: LineSegment StartX=8.57622 StartY=-1.04107 StartZ=0 EndX=8.51407 EndY=-1.12264 EndZ=0
    g195: LineSegment StartX=8.51407 StartY=-1.12264 StartZ=0 EndX=8.42387 EndY=-1.17597 EndZ=0
    g196: LineSegment StartX=8.42387 StartY=-1.17597 StartZ=0 EndX=8.59904 EndY=-1.52027 EndZ=0
    g197: LineSegment StartX=8.59904 StartY=-1.52027 StartZ=0 EndX=8.60604 EndY=-1.53693 EndZ=0
    g198: LineSegment StartX=8.60604 StartY=-1.53693 StartZ=0 EndX=8.6091 EndY=-1.55449 EndZ=0
    g199: LineSegment StartX=8.6091 StartY=-1.55449 StartZ=0 EndX=8.5947 EndY=-1.59042 EndZ=0
    g200: LineSegment StartX=8.5947 StartY=-1.59042 StartZ=0 EndX=8.55944 EndY=-1.6055 EndZ=0
    g201: LineSegment StartX=8.55944 StartY=-1.6055 StartZ=0 EndX=8.53245 EndY=-1.5936 EndZ=0
    g202: LineSegment StartX=8.53245 StartY=-1.5936 StartZ=0 EndX=8.51447 EndY=-1.56724 EndZ=0
    g203: LineSegment StartX=8.51447 StartY=-1.56724 StartZ=0 EndX=8.32655 EndY=-1.20013 EndZ=0
    g204: LineSegment StartX=8.32655 StartY=-1.20013 StartZ=0 EndX=8.09904 EndY=-1.20013 EndZ=0
    g205: LineSegment StartX=8.09904 StartY=-1.20013 StartZ=0 EndX=8.09904 EndY=-1.55248 EndZ=0
    g206: LineSegment StartX=8.09904 StartY=-1.55248 StartZ=0 EndX=8.08512 EndY=-1.58957 EndZ=0
    g207: LineSegment StartX=8.08512 StartY=-1.58957 StartZ=0 EndX=8.05004 EndY=-1.6055 EndZ=0
    g208: LineSegment StartX=8.05004 StartY=-1.6055 StartZ=0 EndX=8.01569 EndY=-1.58918 EndZ=0
    g209: LineSegment StartX=8.01569 StartY=-1.58918 StartZ=0 EndX=8.00239 EndY=-1.55181 EndZ=0
    g210: LineSegment StartX=8.00239 StartY=-1.55181 StartZ=0 EndX=8.00239 EndY=-0.647782 EndZ=0
    g211: LineSegment StartX=8.00239 StartY=-0.647782 StartZ=0 EndX=8.01779 EndY=-0.61117 EndZ=0
    g212: LineSegment StartX=8.01779 StartY=-0.61117 StartZ=0 EndX=8.05474 EndY=-0.596104 EndZ=0
    g213: LineSegment StartX=8.10105 StartY=-0.692077 StartZ=0 EndX=8.10105 EndY=-1.10147 EndZ=0
    g214: LineSegment StartX=8.10105 StartY=-1.10147 StartZ=0 EndX=8.1018 EndY=-1.0941 EndZ=0
    g215: LineSegment StartX=8.1018 StartY=-1.0941 StartZ=0 EndX=8.32051 EndY=-1.10147 EndZ=0
    g216: LineSegment StartX=8.32051 StartY=-1.10147 StartZ=0 EndX=8.39585 EndY=-1.0821 EndZ=0
    g217: LineSegment StartX=8.39585 StartY=-1.0821 StartZ=0 EndX=8.46011 EndY=-1.03503 EndZ=0
    g218: LineSegment StartX=8.46011 StartY=-1.03503 StartZ=0 EndX=8.50199 EndY=-0.968517 EndZ=0
    g219: LineSegment StartX=8.50199 StartY=-0.968517 StartZ=0 EndX=8.51447 EndY=-0.889393 EndZ=0
    g220: LineSegment StartX=8.51447 StartY=-0.889393 StartZ=0 EndX=8.49801 EndY=-0.818001 EndZ=0
    g221: LineSegment StartX=8.49801 StartY=-0.818001 StartZ=0 EndX=8.45541 EndY=-0.757178 EndZ=0
    g222: LineSegment StartX=8.45541 StartY=-0.757178 StartZ=0 EndX=8.39366 EndY=-0.710478 EndZ=0
    g223: LineSegment StartX=8.39366 StartY=-0.710478 StartZ=0 EndX=8.31984 EndY=-0.692077 EndZ=0
    g224: LineSegment StartX=8.31984 StartY=-0.692077 StartZ=0 EndX=8.10105 EndY=-0.692077 EndZ=0
FEATURE [Sketcher::SketchObject] Sketch038  label="Dwgs-2_0.05"
  FullyConstrained = false
  Placement = pos=(0,0,0.1) rot=(0,0,1;0rad)
  sketch-geometry (41):
    g0: LineSegment StartX=-2.1 StartY=-2 StartZ=0 EndX=-2.1 EndY=-1.5 EndZ=0
    g1: ArcOfCircle CenterX=-1.9 CenterY=-1.5 CenterZ=0 NormalX=0 NormalY=0 NormalZ=1 AngleXU=0 Radius=0.2 StartAngle=1.5708 EndAngle=3.14159
    g2: ArcOfCircle CenterX=-1.9 CenterY=-1.1 CenterZ=0 NormalX=0 NormalY=0 NormalZ=1 AngleXU=0 Radius=0.2 StartAngle=4.71239 EndAngle=6.28319
    g3: LineSegment StartX=-1.7 StartY=-1.1 StartZ=0 EndX=-1.7 EndY=-0.75 EndZ=0
    g4: ArcOfCircle CenterX=-1.9 CenterY=-0.75 CenterZ=0 NormalX=0 NormalY=0 NormalZ=1 AngleXU=0 Radius=0.2 StartAngle=0 EndAngle=1.5708
    g5: LineSegment StartX=-1.9 StartY=-0.55 StartZ=0 EndX=-2.22 EndY=-0.55 EndZ=0
    g6: ArcOfCircle CenterX=-2.22 CenterY=-0.35 CenterZ=0 NormalX=0 NormalY=0 NormalZ=1 AngleXU=0 Radius=0.2 StartAngle=2.34728 EndAngle=4.71239
    g7: LineSegment StartX=-2.36015 StartY=-0.207323 StartZ=0 EndX=-2.25835 EndY=-0.107323 EndZ=0
    g8: ArcOfCircle CenterX=-2.1182 CenterY=-0.25 CenterZ=0 NormalX=0 NormalY=0 NormalZ=1 AngleXU=0 Radius=0.2 StartAngle=1.5708 EndAngle=2.34728
    g9: ArcOfCircle CenterX=-2 CenterY=0.15 CenterZ=0 NormalX=0 NormalY=0 NormalZ=1 AngleXU=0 Radius=0.2 StartAngle=4.71239 EndAngle=6.28319
    g10: LineSegment StartX=-1.8 StartY=0.15 StartZ=0 EndX=-1.8 EndY=0.9 EndZ=0
    g11: ArcOfCircle CenterX=-1.6 CenterY=0.9 CenterZ=0 NormalX=0 NormalY=0 NormalZ=1 AngleXU=0 Radius=0.2 StartAngle=1.5708 EndAngle=3.14159
    g12: LineSegment StartX=-1.6 StartY=1.1 StartZ=0 EndX=1.6 EndY=1.1 EndZ=0
    g13: ArcOfCircle CenterX=1.6 CenterY=0.9 CenterZ=0 NormalX=0 NormalY=0 NormalZ=1 AngleXU=0 Radius=0.2 StartAngle=0 EndAngle=1.5708
    g14: LineSegment StartX=1.8 StartY=0.9 StartZ=0 EndX=1.8 EndY=0.15 EndZ=0
    g15: ArcOfCircle CenterX=2 CenterY=0.15 CenterZ=0 NormalX=0 NormalY=0 NormalZ=1 AngleXU=0 Radius=0.2 StartAngle=3.14159 EndAngle=4.71239
    g16: LineSegment StartX=2 StartY=-0.05 StartZ=0 EndX=2.1182 EndY=-0.05 EndZ=0
    g17: ArcOfCircle CenterX=2.1182 CenterY=-0.25 CenterZ=0 NormalX=0 NormalY=0 NormalZ=1 AngleXU=0 Radius=0.2 StartAngle=0.794317 EndAngle=1.5708
    g18: LineSegment StartX=2.25835 StartY=-0.107323 StartZ=0 EndX=2.36015 EndY=-0.207323 EndZ=0
    g19: ArcOfCircle CenterX=2.22 CenterY=-0.35 CenterZ=0 NormalX=0 NormalY=0 NormalZ=1 AngleXU=0 Radius=0.2 StartAngle=4.71239 EndAngle=7.0775
    g20: LineSegment StartX=2.22 StartY=-0.55 StartZ=0 EndX=1.9 EndY=-0.55 EndZ=0
    g21: ArcOfCircle CenterX=1.9 CenterY=-0.75 CenterZ=0 NormalX=0 NormalY=0 NormalZ=1 AngleXU=0 Radius=0.2 StartAngle=1.5708 EndAngle=3.14159
    g22: LineSegment StartX=1.7 StartY=-1.1 StartZ=0 EndX=1.7 EndY=-0.75 EndZ=0
    g23: ArcOfCircle CenterX=1.9 CenterY=-1.1 CenterZ=0 NormalX=0 NormalY=0 NormalZ=1 AngleXU=0 Radius=0.2 StartAngle=3.14159 EndAngle=4.71239
    g24: ArcOfCircle CenterX=1.9 CenterY=-1.5 CenterZ=0 NormalX=0 NormalY=0 NormalZ=1 AngleXU=0 Radius=0.2 StartAngle=0 EndAngle=1.5708
    g25: LineSegment StartX=2.1 StartY=-1.5 StartZ=0 EndX=2.1 EndY=-2 EndZ=0
    g26: LineSegment StartX=-2.42 StartY=0.15 StartZ=0 EndX=-2.42 EndY=-0.85 EndZ=0
    g27: LineSegment StartX=2.42 StartY=0.15 StartZ=0 EndX=2.42 EndY=-0.85 EndZ=0
    g28: LineSegment StartX=-2.1182 StartY=-0.05 StartZ=0 EndX=-2 EndY=-0.05 EndZ=0
    g29: LineSegment StartX=2.25835 StartY=-0.107323 StartZ=0 EndX=2.2 EndY=-0.05 EndZ=0
    g30: LineSegment StartX=2.1182 StartY=-0.05 StartZ=0 EndX=2.2 EndY=-0.05 EndZ=0
    g31: LineSegment StartX=-2.25835 StartY=-0.107323 StartZ=0 EndX=-2.2 EndY=-0.05 EndZ=0
    g32: LineSegment StartX=-2.1182 StartY=-0.05 StartZ=0 EndX=-2.2 EndY=-0.05 EndZ=0
    g33: LineSegment StartX=-2.1 StartY=-2 StartZ=0 EndX=2.1 EndY=-2 EndZ=0
    g34: LineSegment StartX=-2.22 StartY=-0.55 StartZ=0 EndX=1.8 EndY=0.9 EndZ=0
    g35: LineSegment StartX=-1.8 StartY=0.15 StartZ=0 EndX=0.833793 EndY=1.1 EndZ=0
    g36: LineSegment StartX=-1.70572 StartY=-1.1475 StartZ=0 EndX=1.80259 EndY=0.117932 EndZ=0
    g37: LineSegment StartX=-2.1 StartY=-2 StartZ=0 EndX=1.75914 EndY=-0.608023 EndZ=0
    g38: LineSegment StartX=1.92 StartY=-0.55 StartZ=0 EndX=2.42 EndY=-0.369652 EndZ=0
    g39: LineSegment StartX=-0.327323 StartY=-2 StartZ=0 EndX=1.76325 EndY=-1.24594 EndZ=0
    g40: LineSegment StartX=-1.8 StartY=0.785276 StartZ=0 EndX=-0.927454 EndY=1.1 EndZ=0
  constraints (107):
    c: Vertical(g0)
    c: Vertical(g3)
    c: Horizontal(g5)
    c: Coincident(g8,g7)
    c: Vertical(g10)
    c: Vertical(g14)
    c: Horizontal(g16)
    c: Vertical(g22)
    c: Vertical(g25)
    c: Equal(g25,g0)
    c: Equal(g1,g24)
    c: Equal(g3,g22)
    c: Equal(g5,g20)
    c: Horizontal(g20)
    c: Equal(g18,g7)
    c: Equal(g17,g8)
    c: Equal(g9,g15)
    c: Radius(g1) = 0.2
    c: Equal(g1,g2)
    c: Equal(g2,g4)
    c: Equal(g4,g6)
    c: Equal(g8,g9)
    c: Equal(g11,g24)
    c: Equal(g24,g23)
    c: Equal(g23,g21)
    c: Equal(g21,g19)
    c: Equal(g19,g17)
    c: Tangent(g11,g12) = 1.5708
    c: Tangent(g10,g11) = 1.5708
    c: Tangent(g12,g13) = 1.5708
    c: Tangent(g13,g14) = 1.5708
    c: DistanceX(g10,g13) = 3.6
    c: Tangent(g14,g15) = -1.5708
    c: Tangent(g9,g10) = -1.5708
    c: DistanceY(g15,g12) = 1.15
    c: Symmetric(g11,g12,g-2)
    c: Tangent(g16,g17) = 1.5708
    c: Tangent(g17,g18) = 1.5708
    c: Tangent(g4,g5) = -1.5708
    c: Tangent(g3,g4) = -1.5708
    c: Tangent(g21,g22) = 1.5708
    c: Tangent(g20,g21) = -1.5708
    c: Tangent(g15,g16) = -1.5708
    c: DistanceX(g0,g25) = 4.2
    c: Tangent(g18,g19) = 1.5708
    c: Tangent(g19,g20) = 1.5708
    c: Tangent(g6,g7) = 1.5708
    c: Tangent(g5,g6) = 1.5708
    c: DistanceX(g3,g21) = 3.4
    c: Tangent(g2,g3) = -1.5708
    c: Tangent(g22,g23) = 1.5708
    c: Tangent(g23,g24) = 1.5708
    c: Tangent(g24,g25) = 1.5708
    c: Angle(g2) = 1.5708
    c: Tangent(g1,g2) = 1.5708
    c: Symmetric(g2,g23,g-2)
    c: Tangent(g0,g1) = 1.5708
    c: DistanceY(g5,g11) = 1.65
    c: Angle(g9) = 1.5708
    c: Symmetric(g9,g15,g-2)
    c: Vertical(g26)
    c: Vertical(g27)
    c: Equal(g26,g27)
    c: DistanceX(g26,g27) = 4.84
    c: Symmetric(g26,g27,g-2)
    c: Tangent(g6,g26)
    c: DistanceY(g23,g12) = 2.4
    c: DistanceY(g6,g26) = 0.5
    c: DistanceY(g26,g26) = 1
    c: DistanceY(g0,g0) = 0.5
    c: Coincident(g28,g8)
    c: Coincident(g28,g9)
    c: Horizontal(g28)
    c: Coincident(g29,g17)
    c: Tangent(g29,g17)
    c: Coincident(g30,g16)
    c: Coincident(g30,g29)
    c: Parallel(g30,g16)
    c: Coincident(g31,g7)
    c: Coincident(g32,g8)
    c: Coincident(g32,g31)
    c: Parallel(g31,g7)
    c: DistanceX(g31,g29) = 4.4
    c: Symmetric(g31,g29,g-2)
    c: Equal(g28,g16)
    c: DistanceY(g-1,g11) = 1.1
    c: Coincident(g33,g0)
    c: Coincident(g33,g25)
    c: Coincident(g34,g5)
    c: Coincident(g34,g13)
    c: Coincident(g35,g9)
    c: PointOnObject(g36,g2)
    c: Coincident(g37,g0)
    c: Angle(g35,g34) = 0
    c: PointOnObject(g35,g12)
    c: Angle(g34,g36) = 0
    c: PointOnObject(g36,g15)
    c: Angle(g36,g37) = 0
    c: PointOnObject(g37,g21)
    c: PointOnObject(g38,g20)
    c: PointOnObject(g38,g27)
    c: Angle(g37,g39) = 0
    c: PointOnObject(g39,g33)
    c: PointOnObject(g39,g23)
    c: Angle(g40,g35) = 0
    c: PointOnObject(g40,g12)
    c: PointOnObject(g40,g10)
FEATURE [App::DocumentObjectGroup] Group  label="fp-flat-cable"
  Group = -> [Sketch,Sketch003,Sketch006,Sketch007,Sketch008,Sketch009,Sketch010,Sketch011,Sketch012,Sketch013,Sketch014,Sketch005,Sketch022,Sketch029,Sketch030,Sketch031,Sketch038,Text,Text001]
